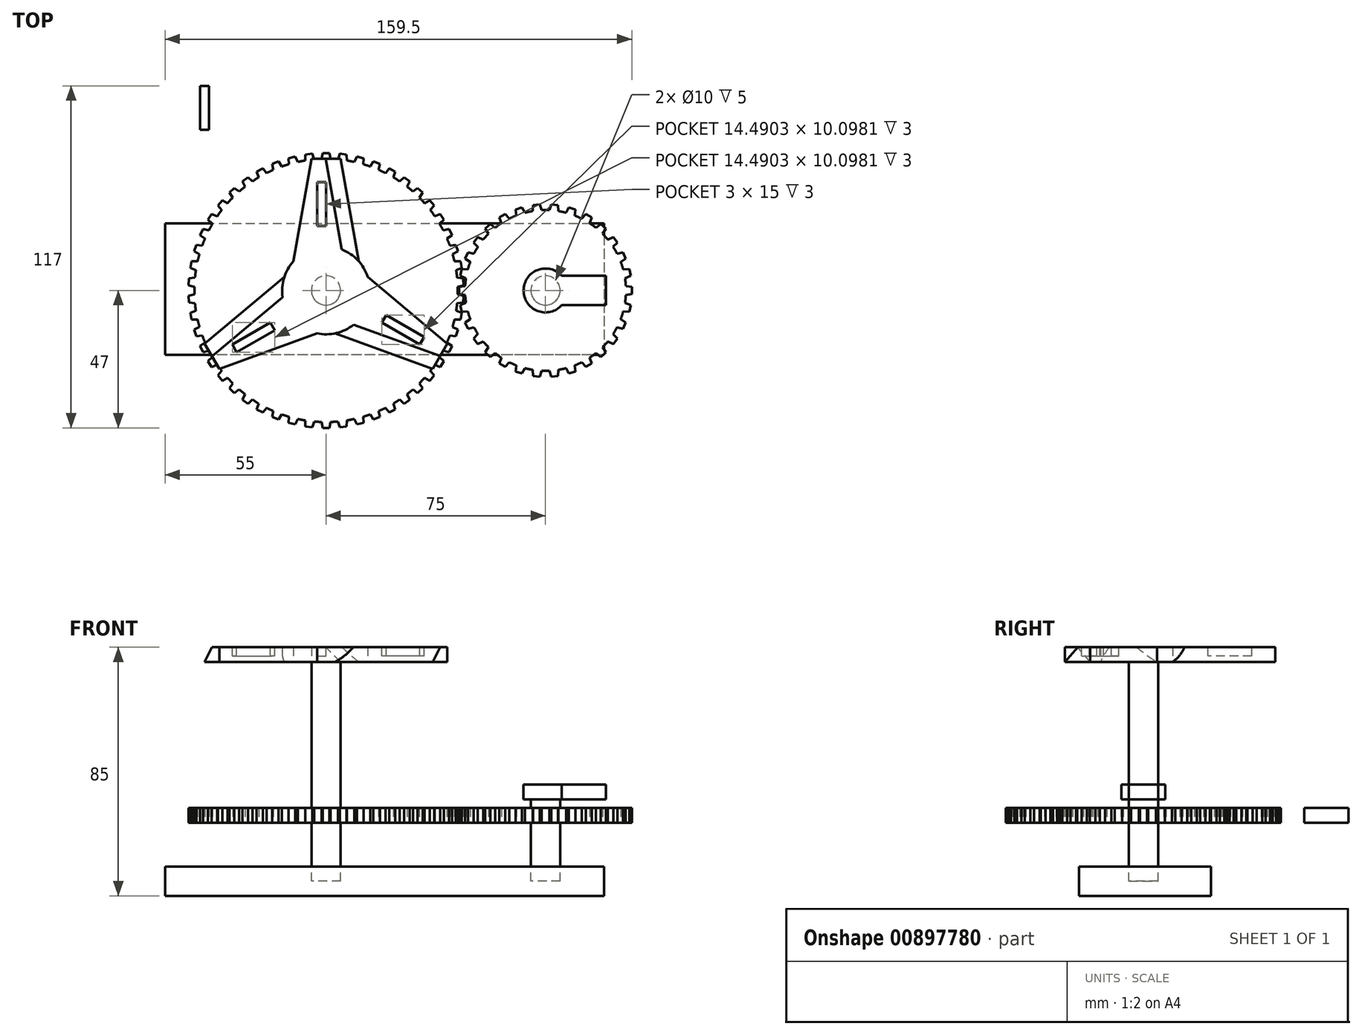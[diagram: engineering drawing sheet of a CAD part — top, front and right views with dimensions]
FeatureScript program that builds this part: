
annotation { "Feature Type Name" : "Feature", "Feature Type Description" : "" }
export const myFeature = defineFeature(function(context is Context, id is Id, definition is map)
    precondition{}
    {
        {
            var Q0;
            Q0=qCreatedBy(makeId("Top.planeOp"),FACE);
            var sketch = newSketch(context, id + "F0", { "sketchPlane" : qUnion([Q0])});
            skCircle(sketch, "E0", {"center": v(0, 0) * mm, "radius": 45 * mm});
            skLineSegment(sketch, "E1", {"start": v(0, 47) * mm, "end": v(1.18, 47) * mm});
            skLineSegment(sketch, "E2", {"start": v(1.18, 47) * mm, "end": v(1.54, 44.97) * mm});
            skLineSegment(sketch, "E3.MirrorCS", {"start": v(0, 47) * mm, "end": v(-1.18, 47) * mm});
            skLineSegment(sketch, "E4.MirrorCS", {"start": v(-1.18, 47) * mm, "end": v(-1.54, 44.97) * mm});
            skLineSegment(sketch, "E5.1.0", {"start": v(-7.06, 46.48) * mm, "end": v(-7.16, 44.43) * mm});
            skLineSegment(sketch, "E5.1.1", {"start": v(-5.9, 46.63) * mm, "end": v(-7.06, 46.48) * mm});
            skLineSegment(sketch, "E5.1.2", {"start": v(-5.9, 46.63) * mm, "end": v(-4.72, 46.78) * mm});
            skLineSegment(sketch, "E5.1.3", {"start": v(-4.72, 46.78) * mm, "end": v(-4.11, 44.81) * mm});
            skLineSegment(sketch, "E5.2.0", {"start": v(-12.83, 45.23) * mm, "end": v(-12.67, 43.18) * mm});
            skLineSegment(sketch, "E5.2.1", {"start": v(-11.69, 45.52) * mm, "end": v(-12.83, 45.23) * mm});
            skLineSegment(sketch, "E5.2.2", {"start": v(-11.69, 45.52) * mm, "end": v(-10.55, 45.82) * mm});
            skLineSegment(sketch, "E5.2.3", {"start": v(-10.55, 45.82) * mm, "end": v(-9.7, 43.94) * mm});
            skLineSegment(sketch, "E6.2.3.0", {"start": v(-18.4, 43.27) * mm, "end": v(-17.98, 41.25) * mm});
            skLineSegment(sketch, "E6.3.3.0", {"start": v(-17.3, 43.7) * mm, "end": v(-18.4, 43.27) * mm});
            skLineSegment(sketch, "E6.6.3.0", {"start": v(-17.3, 43.7) * mm, "end": v(-16.2, 44.13) * mm});
            skLineSegment(sketch, "E6.9.3.0", {"start": v(-16.2, 44.13) * mm, "end": v(-15.13, 42.38) * mm});
            skLineSegment(sketch, "E6.2.4.0", {"start": v(-23.67, 40.62) * mm, "end": v(-23.01, 38.67) * mm});
            skLineSegment(sketch, "E6.3.4.0", {"start": v(-22.64, 41.19) * mm, "end": v(-23.67, 40.62) * mm});
            skLineSegment(sketch, "E6.6.4.0", {"start": v(-22.64, 41.19) * mm, "end": v(-21.61, 41.75) * mm});
            skLineSegment(sketch, "E6.9.4.0", {"start": v(-21.61, 41.75) * mm, "end": v(-20.32, 40.15) * mm});
            skLineSegment(sketch, "E6.2.5.0", {"start": v(-28.58, 37.33) * mm, "end": v(-27.68, 35.48) * mm});
            skLineSegment(sketch, "E6.3.5.0", {"start": v(-27.63, 38.02) * mm, "end": v(-28.58, 37.33) * mm});
            skLineSegment(sketch, "E6.6.5.0", {"start": v(-27.63, 38.02) * mm, "end": v(-26.67, 38.72) * mm});
            skLineSegment(sketch, "E6.9.5.0", {"start": v(-26.67, 38.72) * mm, "end": v(-25.2, 37.29) * mm});
            skLineSegment(sketch, "E6.2.6.0", {"start": v(-33.03, 33.46) * mm, "end": v(-31.9, 31.73) * mm});
            skLineSegment(sketch, "E6.3.6.0", {"start": v(-32.17, 34.26) * mm, "end": v(-33.03, 33.46) * mm});
            skLineSegment(sketch, "E6.6.6.0", {"start": v(-32.17, 34.26) * mm, "end": v(-31.31, 35.07) * mm});
            skLineSegment(sketch, "E6.9.6.0", {"start": v(-31.31, 35.07) * mm, "end": v(-29.67, 33.84) * mm});
            skLineSegment(sketch, "E6.2.7.0", {"start": v(-36.97, 29.05) * mm, "end": v(-35.63, 27.48) * mm});
            skLineSegment(sketch, "E6.3.7.0", {"start": v(-36.21, 29.96) * mm, "end": v(-36.97, 29.05) * mm});
            skLineSegment(sketch, "E6.6.7.0", {"start": v(-36.21, 29.96) * mm, "end": v(-35.46, 30.87) * mm});
            skLineSegment(sketch, "E6.9.7.0", {"start": v(-35.46, 30.87) * mm, "end": v(-33.67, 29.85) * mm});
            skLineSegment(sketch, "E6.2.8.0", {"start": v(-40.31, 24.19) * mm, "end": v(-38.8, 22.8) * mm});
            skLineSegment(sketch, "E6.3.8.0", {"start": v(-39.68, 25.18) * mm, "end": v(-40.31, 24.19) * mm});
            skLineSegment(sketch, "E6.6.8.0", {"start": v(-39.68, 25.18) * mm, "end": v(-39.05, 26.18) * mm});
            skLineSegment(sketch, "E6.9.8.0", {"start": v(-39.05, 26.18) * mm, "end": v(-37.15, 25.4) * mm});
            skLineSegment(sketch, "E6.2.9.0", {"start": v(-43.03, 18.95) * mm, "end": v(-41.35, 17.76) * mm});
            skLineSegment(sketch, "E6.3.9.0", {"start": v(-42.53, 20.01) * mm, "end": v(-43.03, 18.95) * mm});
            skLineSegment(sketch, "E6.6.9.0", {"start": v(-42.53, 20.01) * mm, "end": v(-42.03, 21.08) * mm});
            skLineSegment(sketch, "E6.9.9.0", {"start": v(-42.03, 21.08) * mm, "end": v(-40.04, 20.54) * mm});
            skLineSegment(sketch, "E6.2.10.0", {"start": v(-45.06, 13.4) * mm, "end": v(-43.25, 12.44) * mm});
            skLineSegment(sketch, "E6.3.10.0", {"start": v(-44.7, 14.52) * mm, "end": v(-45.06, 13.4) * mm});
            skLineSegment(sketch, "E6.6.10.0", {"start": v(-44.7, 14.52) * mm, "end": v(-44.34, 15.64) * mm});
            skLineSegment(sketch, "E6.9.10.0", {"start": v(-44.34, 15.64) * mm, "end": v(-42.3, 15.36) * mm});
            skLineSegment(sketch, "E6.2.11.0", {"start": v(-46.39, 7.65) * mm, "end": v(-44.46, 6.92) * mm});
            skLineSegment(sketch, "E6.3.11.0", {"start": v(-46.17, 8.8) * mm, "end": v(-46.39, 7.65) * mm});
            skLineSegment(sketch, "E6.6.11.0", {"start": v(-46.17, 8.8) * mm, "end": v(-45.95, 9.96) * mm});
            skLineSegment(sketch, "E6.9.11.0", {"start": v(-45.95, 9.96) * mm, "end": v(-43.89, 9.94) * mm});
            skLineSegment(sketch, "E6.2.12.0", {"start": v(-46.98, 1.78) * mm, "end": v(-44.98, 1.3) * mm});
            skLineSegment(sketch, "E6.3.12.0", {"start": v(-46.9, 2.95) * mm, "end": v(-46.98, 1.78) * mm});
            skLineSegment(sketch, "E6.6.12.0", {"start": v(-46.9, 2.95) * mm, "end": v(-46.83, 4.13) * mm});
            skLineSegment(sketch, "E6.9.12.0", {"start": v(-46.83, 4.13) * mm, "end": v(-44.79, 4.36) * mm});
            skLineSegment(sketch, "E6.2.13.0", {"start": v(-46.83, -4.13) * mm, "end": v(-44.79, -4.36) * mm});
            skLineSegment(sketch, "E6.3.13.0", {"start": v(-46.9, -2.95) * mm, "end": v(-46.83, -4.13) * mm});
            skLineSegment(sketch, "E6.6.13.0", {"start": v(-46.9, -2.95) * mm, "end": v(-46.98, -1.78) * mm});
            skLineSegment(sketch, "E6.9.13.0", {"start": v(-46.98, -1.78) * mm, "end": v(-44.98, -1.3) * mm});
            skLineSegment(sketch, "E6.2.14.0", {"start": v(-45.95, -9.96) * mm, "end": v(-43.89, -9.94) * mm});
            skLineSegment(sketch, "E6.3.14.0", {"start": v(-46.17, -8.8) * mm, "end": v(-45.95, -9.96) * mm});
            skLineSegment(sketch, "E6.6.14.0", {"start": v(-46.17, -8.8) * mm, "end": v(-46.39, -7.65) * mm});
            skLineSegment(sketch, "E6.9.14.0", {"start": v(-46.39, -7.65) * mm, "end": v(-44.46, -6.92) * mm});
            skLineSegment(sketch, "E6.2.15.0", {"start": v(-44.34, -15.64) * mm, "end": v(-42.3, -15.36) * mm});
            skLineSegment(sketch, "E6.3.15.0", {"start": v(-44.7, -14.52) * mm, "end": v(-44.34, -15.64) * mm});
            skLineSegment(sketch, "E6.6.15.0", {"start": v(-44.7, -14.52) * mm, "end": v(-45.06, -13.4) * mm});
            skLineSegment(sketch, "E6.9.15.0", {"start": v(-45.06, -13.4) * mm, "end": v(-43.25, -12.44) * mm});
            skLineSegment(sketch, "E6.2.16.0", {"start": v(-42.03, -21.08) * mm, "end": v(-40.04, -20.54) * mm});
            skLineSegment(sketch, "E6.3.16.0", {"start": v(-42.53, -20.01) * mm, "end": v(-42.03, -21.08) * mm});
            skLineSegment(sketch, "E6.6.16.0", {"start": v(-42.53, -20.01) * mm, "end": v(-43.03, -18.95) * mm});
            skLineSegment(sketch, "E6.9.16.0", {"start": v(-43.03, -18.95) * mm, "end": v(-41.35, -17.76) * mm});
            skLineSegment(sketch, "E6.2.17.0", {"start": v(-39.05, -26.18) * mm, "end": v(-37.15, -25.4) * mm});
            skLineSegment(sketch, "E6.3.17.0", {"start": v(-39.68, -25.18) * mm, "end": v(-39.05, -26.18) * mm});
            skLineSegment(sketch, "E6.6.17.0", {"start": v(-39.68, -25.18) * mm, "end": v(-40.31, -24.19) * mm});
            skLineSegment(sketch, "E6.9.17.0", {"start": v(-40.31, -24.19) * mm, "end": v(-38.8, -22.8) * mm});
            skLineSegment(sketch, "E6.2.18.0", {"start": v(-35.46, -30.87) * mm, "end": v(-33.67, -29.85) * mm});
            skLineSegment(sketch, "E6.3.18.0", {"start": v(-36.21, -29.96) * mm, "end": v(-35.46, -30.87) * mm});
            skLineSegment(sketch, "E6.6.18.0", {"start": v(-36.21, -29.96) * mm, "end": v(-36.97, -29.05) * mm});
            skLineSegment(sketch, "E6.9.18.0", {"start": v(-36.97, -29.05) * mm, "end": v(-35.63, -27.48) * mm});
            skLineSegment(sketch, "E6.2.19.0", {"start": v(-31.31, -35.07) * mm, "end": v(-29.67, -33.84) * mm});
            skLineSegment(sketch, "E6.3.19.0", {"start": v(-32.17, -34.26) * mm, "end": v(-31.31, -35.07) * mm});
            skLineSegment(sketch, "E6.6.19.0", {"start": v(-32.17, -34.26) * mm, "end": v(-33.03, -33.46) * mm});
            skLineSegment(sketch, "E6.9.19.0", {"start": v(-33.03, -33.46) * mm, "end": v(-31.9, -31.73) * mm});
            skLineSegment(sketch, "E6.2.20.0", {"start": v(-26.67, -38.72) * mm, "end": v(-25.2, -37.29) * mm});
            skLineSegment(sketch, "E6.3.20.0", {"start": v(-27.63, -38.02) * mm, "end": v(-26.67, -38.72) * mm});
            skLineSegment(sketch, "E6.6.20.0", {"start": v(-27.63, -38.02) * mm, "end": v(-28.58, -37.33) * mm});
            skLineSegment(sketch, "E6.9.20.0", {"start": v(-28.58, -37.33) * mm, "end": v(-27.68, -35.48) * mm});
            skLineSegment(sketch, "E6.2.21.0", {"start": v(-21.61, -41.75) * mm, "end": v(-20.32, -40.15) * mm});
            skLineSegment(sketch, "E6.3.21.0", {"start": v(-22.64, -41.19) * mm, "end": v(-21.61, -41.75) * mm});
            skLineSegment(sketch, "E6.6.21.0", {"start": v(-22.64, -41.19) * mm, "end": v(-23.67, -40.62) * mm});
            skLineSegment(sketch, "E6.9.21.0", {"start": v(-23.67, -40.62) * mm, "end": v(-23.01, -38.67) * mm});
            skLineSegment(sketch, "E6.2.22.0", {"start": v(-16.2, -44.13) * mm, "end": v(-15.13, -42.38) * mm});
            skLineSegment(sketch, "E6.3.22.0", {"start": v(-17.3, -43.7) * mm, "end": v(-16.2, -44.13) * mm});
            skLineSegment(sketch, "E6.6.22.0", {"start": v(-17.3, -43.7) * mm, "end": v(-18.4, -43.27) * mm});
            skLineSegment(sketch, "E6.9.22.0", {"start": v(-18.4, -43.27) * mm, "end": v(-17.98, -41.25) * mm});
            skLineSegment(sketch, "E6.2.23.0", {"start": v(-10.55, -45.82) * mm, "end": v(-9.7, -43.94) * mm});
            skLineSegment(sketch, "E6.3.23.0", {"start": v(-11.69, -45.52) * mm, "end": v(-10.55, -45.82) * mm});
            skLineSegment(sketch, "E6.6.23.0", {"start": v(-11.69, -45.52) * mm, "end": v(-12.83, -45.23) * mm});
            skLineSegment(sketch, "E6.9.23.0", {"start": v(-12.83, -45.23) * mm, "end": v(-12.67, -43.18) * mm});
            skLineSegment(sketch, "E6.2.24.0", {"start": v(-4.72, -46.78) * mm, "end": v(-4.11, -44.81) * mm});
            skLineSegment(sketch, "E6.3.24.0", {"start": v(-5.9, -46.63) * mm, "end": v(-4.72, -46.78) * mm});
            skLineSegment(sketch, "E6.6.24.0", {"start": v(-5.9, -46.63) * mm, "end": v(-7.06, -46.48) * mm});
            skLineSegment(sketch, "E6.9.24.0", {"start": v(-7.06, -46.48) * mm, "end": v(-7.16, -44.43) * mm});
            skLineSegment(sketch, "E6.2.25.0", {"start": v(1.18, -47) * mm, "end": v(1.54, -44.97) * mm});
            skLineSegment(sketch, "E6.3.25.0", {"start": v(0, -47) * mm, "end": v(1.18, -47) * mm});
            skLineSegment(sketch, "E6.6.25.0", {"start": v(0, -47) * mm, "end": v(-1.18, -47) * mm});
            skLineSegment(sketch, "E6.9.25.0", {"start": v(-1.18, -47) * mm, "end": v(-1.54, -44.97) * mm});
            skLineSegment(sketch, "E6.2.26.0", {"start": v(7.06, -46.48) * mm, "end": v(7.16, -44.43) * mm});
            skLineSegment(sketch, "E6.3.26.0", {"start": v(5.9, -46.63) * mm, "end": v(7.06, -46.48) * mm});
            skLineSegment(sketch, "E6.6.26.0", {"start": v(5.9, -46.63) * mm, "end": v(4.72, -46.78) * mm});
            skLineSegment(sketch, "E6.9.26.0", {"start": v(4.72, -46.78) * mm, "end": v(4.11, -44.81) * mm});
            skLineSegment(sketch, "E6.2.27.0", {"start": v(12.83, -45.23) * mm, "end": v(12.67, -43.18) * mm});
            skLineSegment(sketch, "E6.3.27.0", {"start": v(11.69, -45.52) * mm, "end": v(12.83, -45.23) * mm});
            skLineSegment(sketch, "E6.6.27.0", {"start": v(11.69, -45.52) * mm, "end": v(10.55, -45.82) * mm});
            skLineSegment(sketch, "E6.9.27.0", {"start": v(10.55, -45.82) * mm, "end": v(9.7, -43.94) * mm});
            skLineSegment(sketch, "E6.2.28.0", {"start": v(18.4, -43.27) * mm, "end": v(17.98, -41.25) * mm});
            skLineSegment(sketch, "E6.3.28.0", {"start": v(17.3, -43.7) * mm, "end": v(18.4, -43.27) * mm});
            skLineSegment(sketch, "E6.6.28.0", {"start": v(17.3, -43.7) * mm, "end": v(16.2, -44.13) * mm});
            skLineSegment(sketch, "E6.9.28.0", {"start": v(16.2, -44.13) * mm, "end": v(15.13, -42.38) * mm});
            skLineSegment(sketch, "E6.2.29.0", {"start": v(23.67, -40.62) * mm, "end": v(23.01, -38.67) * mm});
            skLineSegment(sketch, "E6.3.29.0", {"start": v(22.64, -41.19) * mm, "end": v(23.67, -40.62) * mm});
            skLineSegment(sketch, "E6.6.29.0", {"start": v(22.64, -41.19) * mm, "end": v(21.61, -41.75) * mm});
            skLineSegment(sketch, "E6.9.29.0", {"start": v(21.61, -41.75) * mm, "end": v(20.32, -40.15) * mm});
            skLineSegment(sketch, "E7.2.30.0", {"start": v(28.58, -37.33) * mm, "end": v(27.68, -35.48) * mm});
            skLineSegment(sketch, "E7.3.30.0", {"start": v(27.63, -38.02) * mm, "end": v(28.58, -37.33) * mm});
            skLineSegment(sketch, "E7.6.30.0", {"start": v(27.63, -38.02) * mm, "end": v(26.67, -38.72) * mm});
            skLineSegment(sketch, "E7.9.30.0", {"start": v(26.67, -38.72) * mm, "end": v(25.2, -37.29) * mm});
            skLineSegment(sketch, "E7.2.31.0", {"start": v(33.03, -33.46) * mm, "end": v(31.9, -31.73) * mm});
            skLineSegment(sketch, "E7.3.31.0", {"start": v(32.17, -34.26) * mm, "end": v(33.03, -33.46) * mm});
            skLineSegment(sketch, "E7.6.31.0", {"start": v(32.17, -34.26) * mm, "end": v(31.31, -35.07) * mm});
            skLineSegment(sketch, "E7.9.31.0", {"start": v(31.31, -35.07) * mm, "end": v(29.67, -33.84) * mm});
            skLineSegment(sketch, "E7.2.32.0", {"start": v(36.97, -29.05) * mm, "end": v(35.63, -27.48) * mm});
            skLineSegment(sketch, "E7.3.32.0", {"start": v(36.21, -29.96) * mm, "end": v(36.97, -29.05) * mm});
            skLineSegment(sketch, "E7.6.32.0", {"start": v(36.21, -29.96) * mm, "end": v(35.46, -30.87) * mm});
            skLineSegment(sketch, "E7.9.32.0", {"start": v(35.46, -30.87) * mm, "end": v(33.67, -29.85) * mm});
            skLineSegment(sketch, "E7.2.33.0", {"start": v(40.31, -24.19) * mm, "end": v(38.8, -22.8) * mm});
            skLineSegment(sketch, "E7.3.33.0", {"start": v(39.68, -25.18) * mm, "end": v(40.31, -24.19) * mm});
            skLineSegment(sketch, "E7.6.33.0", {"start": v(39.68, -25.18) * mm, "end": v(39.05, -26.18) * mm});
            skLineSegment(sketch, "E7.9.33.0", {"start": v(39.05, -26.18) * mm, "end": v(37.15, -25.4) * mm});
            skLineSegment(sketch, "E7.2.34.0", {"start": v(43.03, -18.95) * mm, "end": v(41.35, -17.76) * mm});
            skLineSegment(sketch, "E7.3.34.0", {"start": v(42.53, -20.01) * mm, "end": v(43.03, -18.95) * mm});
            skLineSegment(sketch, "E7.6.34.0", {"start": v(42.53, -20.01) * mm, "end": v(42.03, -21.08) * mm});
            skLineSegment(sketch, "E7.9.34.0", {"start": v(42.03, -21.08) * mm, "end": v(40.04, -20.54) * mm});
            skLineSegment(sketch, "E7.2.35.0", {"start": v(45.06, -13.4) * mm, "end": v(43.25, -12.44) * mm});
            skLineSegment(sketch, "E7.3.35.0", {"start": v(44.7, -14.52) * mm, "end": v(45.06, -13.4) * mm});
            skLineSegment(sketch, "E7.6.35.0", {"start": v(44.7, -14.52) * mm, "end": v(44.34, -15.64) * mm});
            skLineSegment(sketch, "E7.9.35.0", {"start": v(44.34, -15.64) * mm, "end": v(42.3, -15.36) * mm});
            skLineSegment(sketch, "E7.2.36.0", {"start": v(46.39, -7.65) * mm, "end": v(44.46, -6.92) * mm});
            skLineSegment(sketch, "E7.3.36.0", {"start": v(46.17, -8.8) * mm, "end": v(46.39, -7.65) * mm});
            skLineSegment(sketch, "E7.6.36.0", {"start": v(46.17, -8.8) * mm, "end": v(45.95, -9.96) * mm});
            skLineSegment(sketch, "E7.9.36.0", {"start": v(45.95, -9.96) * mm, "end": v(43.89, -9.94) * mm});
            skLineSegment(sketch, "E7.2.37.0", {"start": v(46.98, -1.78) * mm, "end": v(44.98, -1.3) * mm});
            skLineSegment(sketch, "E7.3.37.0", {"start": v(46.9, -2.95) * mm, "end": v(46.98, -1.78) * mm});
            skLineSegment(sketch, "E7.6.37.0", {"start": v(46.9, -2.95) * mm, "end": v(46.83, -4.13) * mm});
            skLineSegment(sketch, "E7.9.37.0", {"start": v(46.83, -4.13) * mm, "end": v(44.79, -4.36) * mm});
            skLineSegment(sketch, "E7.2.38.0", {"start": v(46.83, 4.13) * mm, "end": v(44.79, 4.36) * mm});
            skLineSegment(sketch, "E7.3.38.0", {"start": v(46.9, 2.95) * mm, "end": v(46.83, 4.13) * mm});
            skLineSegment(sketch, "E7.6.38.0", {"start": v(46.9, 2.95) * mm, "end": v(46.98, 1.78) * mm});
            skLineSegment(sketch, "E7.9.38.0", {"start": v(46.98, 1.78) * mm, "end": v(44.98, 1.3) * mm});
            skLineSegment(sketch, "E7.2.39.0", {"start": v(45.95, 9.96) * mm, "end": v(43.89, 9.94) * mm});
            skLineSegment(sketch, "E7.3.39.0", {"start": v(46.17, 8.8) * mm, "end": v(45.95, 9.96) * mm});
            skLineSegment(sketch, "E7.6.39.0", {"start": v(46.17, 8.8) * mm, "end": v(46.39, 7.65) * mm});
            skLineSegment(sketch, "E7.9.39.0", {"start": v(46.39, 7.65) * mm, "end": v(44.46, 6.92) * mm});
            skLineSegment(sketch, "E7.2.40.0", {"start": v(44.34, 15.64) * mm, "end": v(42.3, 15.36) * mm});
            skLineSegment(sketch, "E7.3.40.0", {"start": v(44.7, 14.52) * mm, "end": v(44.34, 15.64) * mm});
            skLineSegment(sketch, "E7.6.40.0", {"start": v(44.7, 14.52) * mm, "end": v(45.06, 13.4) * mm});
            skLineSegment(sketch, "E7.9.40.0", {"start": v(45.06, 13.4) * mm, "end": v(43.25, 12.44) * mm});
            skLineSegment(sketch, "E7.2.41.0", {"start": v(42.03, 21.08) * mm, "end": v(40.04, 20.54) * mm});
            skLineSegment(sketch, "E7.3.41.0", {"start": v(42.53, 20.01) * mm, "end": v(42.03, 21.08) * mm});
            skLineSegment(sketch, "E7.6.41.0", {"start": v(42.53, 20.01) * mm, "end": v(43.03, 18.95) * mm});
            skLineSegment(sketch, "E7.9.41.0", {"start": v(43.03, 18.95) * mm, "end": v(41.35, 17.76) * mm});
            skLineSegment(sketch, "E7.2.42.0", {"start": v(39.05, 26.18) * mm, "end": v(37.15, 25.4) * mm});
            skLineSegment(sketch, "E7.3.42.0", {"start": v(39.68, 25.18) * mm, "end": v(39.05, 26.18) * mm});
            skLineSegment(sketch, "E7.6.42.0", {"start": v(39.68, 25.18) * mm, "end": v(40.31, 24.19) * mm});
            skLineSegment(sketch, "E7.9.42.0", {"start": v(40.31, 24.19) * mm, "end": v(38.8, 22.8) * mm});
            skLineSegment(sketch, "E7.2.43.0", {"start": v(35.46, 30.87) * mm, "end": v(33.67, 29.85) * mm});
            skLineSegment(sketch, "E7.3.43.0", {"start": v(36.21, 29.96) * mm, "end": v(35.46, 30.87) * mm});
            skLineSegment(sketch, "E7.6.43.0", {"start": v(36.21, 29.96) * mm, "end": v(36.97, 29.05) * mm});
            skLineSegment(sketch, "E7.9.43.0", {"start": v(36.97, 29.05) * mm, "end": v(35.63, 27.48) * mm});
            skLineSegment(sketch, "E7.2.44.0", {"start": v(31.31, 35.07) * mm, "end": v(29.67, 33.84) * mm});
            skLineSegment(sketch, "E7.3.44.0", {"start": v(32.17, 34.26) * mm, "end": v(31.31, 35.07) * mm});
            skLineSegment(sketch, "E7.6.44.0", {"start": v(32.17, 34.26) * mm, "end": v(33.03, 33.46) * mm});
            skLineSegment(sketch, "E7.9.44.0", {"start": v(33.03, 33.46) * mm, "end": v(31.9, 31.73) * mm});
            skLineSegment(sketch, "E7.2.45.0", {"start": v(26.67, 38.72) * mm, "end": v(25.2, 37.29) * mm});
            skLineSegment(sketch, "E7.3.45.0", {"start": v(27.63, 38.02) * mm, "end": v(26.67, 38.72) * mm});
            skLineSegment(sketch, "E7.6.45.0", {"start": v(27.63, 38.02) * mm, "end": v(28.58, 37.33) * mm});
            skLineSegment(sketch, "E7.9.45.0", {"start": v(28.58, 37.33) * mm, "end": v(27.68, 35.48) * mm});
            skLineSegment(sketch, "E7.2.46.0", {"start": v(21.61, 41.75) * mm, "end": v(20.32, 40.15) * mm});
            skLineSegment(sketch, "E7.3.46.0", {"start": v(22.64, 41.19) * mm, "end": v(21.61, 41.75) * mm});
            skLineSegment(sketch, "E7.6.46.0", {"start": v(22.64, 41.19) * mm, "end": v(23.67, 40.62) * mm});
            skLineSegment(sketch, "E7.9.46.0", {"start": v(23.67, 40.62) * mm, "end": v(23.01, 38.67) * mm});
            skLineSegment(sketch, "E7.2.47.0", {"start": v(16.2, 44.13) * mm, "end": v(15.13, 42.38) * mm});
            skLineSegment(sketch, "E7.3.47.0", {"start": v(17.3, 43.7) * mm, "end": v(16.2, 44.13) * mm});
            skLineSegment(sketch, "E7.6.47.0", {"start": v(17.3, 43.7) * mm, "end": v(18.4, 43.27) * mm});
            skLineSegment(sketch, "E7.9.47.0", {"start": v(18.4, 43.27) * mm, "end": v(17.98, 41.25) * mm});
            skLineSegment(sketch, "E7.2.48.0", {"start": v(10.55, 45.82) * mm, "end": v(9.7, 43.94) * mm});
            skLineSegment(sketch, "E7.3.48.0", {"start": v(11.69, 45.52) * mm, "end": v(10.55, 45.82) * mm});
            skLineSegment(sketch, "E7.6.48.0", {"start": v(11.69, 45.52) * mm, "end": v(12.83, 45.23) * mm});
            skLineSegment(sketch, "E7.9.48.0", {"start": v(12.83, 45.23) * mm, "end": v(12.67, 43.18) * mm});
            skLineSegment(sketch, "E7.2.49.0", {"start": v(4.72, 46.78) * mm, "end": v(4.11, 44.81) * mm});
            skLineSegment(sketch, "E7.3.49.0", {"start": v(5.9, 46.63) * mm, "end": v(4.72, 46.78) * mm});
            skLineSegment(sketch, "E7.6.49.0", {"start": v(5.9, 46.63) * mm, "end": v(7.06, 46.48) * mm});
            skLineSegment(sketch, "E7.9.49.0", {"start": v(7.06, 46.48) * mm, "end": v(7.16, 44.43) * mm});
            skSolve(sketch);
        }
        {
            var Q0;
            Q0 = qSketchRegion(id + "F0", true);
            extrude(context, id + "F1", {"entities" : qUnion([Q0]), "depth" : 5 * mm, "offsetDistance" : 25 * mm});
        }
        {
            var Q0;
            Q0=qCreatedBy(makeId("Top.planeOp"),FACE);
            var sketch = newSketch(context, id + "F2", { "sketchPlane" : qUnion([Q0])});
            skCircle(sketch, "E8", {"center": v(75, 0) * mm, "radius": 27.5 * mm});
            skLineSegment(sketch, "E9", {"start": v(45.5, 0) * mm, "end": v(45.5, 1.18) * mm});
            skLineSegment(sketch, "E10", {"start": v(45.5, 1.18) * mm, "end": v(47.54, 1.54) * mm});
            skLineSegment(sketch, "E11.MirrorCS", {"start": v(45.5, 0) * mm, "end": v(45.5, -1.18) * mm});
            skLineSegment(sketch, "E12.MirrorCS", {"start": v(45.5, -1.18) * mm, "end": v(47.54, -1.54) * mm});
            skLineSegment(sketch, "E13.1.0", {"start": v(46.14, -6.13) * mm, "end": v(45.9, -4.98) * mm});
            skLineSegment(sketch, "E13.1.1", {"start": v(45.9, -4.98) * mm, "end": v(47.82, -4.2) * mm});
            skLineSegment(sketch, "E13.1.2", {"start": v(46.14, -6.13) * mm, "end": v(46.39, -7.29) * mm});
            skLineSegment(sketch, "E13.1.3", {"start": v(46.39, -7.29) * mm, "end": v(48.46, -7.21) * mm});
            skLineSegment(sketch, "E14.1.2.0", {"start": v(48.05, -12) * mm, "end": v(47.57, -10.92) * mm});
            skLineSegment(sketch, "E14.3.2.0", {"start": v(47.57, -10.92) * mm, "end": v(49.3, -9.76) * mm});
            skLineSegment(sketch, "E14.6.2.0", {"start": v(48.05, -12) * mm, "end": v(48.53, -13.07) * mm});
            skLineSegment(sketch, "E14.9.2.0", {"start": v(48.53, -13.07) * mm, "end": v(50.54, -12.57) * mm});
            skLineSegment(sketch, "E14.1.3.0", {"start": v(51.13, -17.34) * mm, "end": v(50.44, -16.39) * mm});
            skLineSegment(sketch, "E14.3.3.0", {"start": v(50.44, -16.39) * mm, "end": v(51.88, -14.9) * mm});
            skLineSegment(sketch, "E14.6.3.0", {"start": v(51.13, -17.34) * mm, "end": v(51.83, -18.3) * mm});
            skLineSegment(sketch, "E14.9.3.0", {"start": v(51.83, -18.3) * mm, "end": v(53.7, -17.38) * mm});
            skLineSegment(sketch, "E14.1.4.0", {"start": v(55.26, -21.92) * mm, "end": v(54.39, -21.13) * mm});
            skLineSegment(sketch, "E14.3.4.0", {"start": v(54.39, -21.13) * mm, "end": v(55.48, -19.38) * mm});
            skLineSegment(sketch, "E14.6.4.0", {"start": v(55.26, -21.92) * mm, "end": v(56.14, -22.71) * mm});
            skLineSegment(sketch, "E14.9.4.0", {"start": v(56.14, -22.71) * mm, "end": v(57.77, -21.43) * mm});
            skLineSegment(sketch, "E14.1.5.0", {"start": v(60.25, -25.55) * mm, "end": v(59.23, -24.96) * mm});
            skLineSegment(sketch, "E14.3.5.0", {"start": v(59.23, -24.96) * mm, "end": v(59.94, -23) * mm});
            skLineSegment(sketch, "E14.6.5.0", {"start": v(60.25, -25.55) * mm, "end": v(61.27, -26.14) * mm});
            skLineSegment(sketch, "E14.9.5.0", {"start": v(61.27, -26.14) * mm, "end": v(62.6, -24.55) * mm});
            skLineSegment(sketch, "E14.1.6.0", {"start": v(65.88, -28.06) * mm, "end": v(64.76, -27.7) * mm});
            skLineSegment(sketch, "E14.3.6.0", {"start": v(64.76, -27.7) * mm, "end": v(65.05, -25.64) * mm});
            skLineSegment(sketch, "E14.6.6.0", {"start": v(65.88, -28.06) * mm, "end": v(67, -28.42) * mm});
            skLineSegment(sketch, "E14.9.6.0", {"start": v(67, -28.42) * mm, "end": v(67.98, -26.59) * mm});
            skLineSegment(sketch, "E14.1.7.0", {"start": v(71.92, -29.34) * mm, "end": v(70.74, -29.22) * mm});
            skLineSegment(sketch, "E14.3.7.0", {"start": v(70.74, -29.22) * mm, "end": v(70.6, -27.15) * mm});
            skLineSegment(sketch, "E14.6.7.0", {"start": v(71.92, -29.34) * mm, "end": v(73.09, -29.46) * mm});
            skLineSegment(sketch, "E14.9.7.0", {"start": v(73.09, -29.46) * mm, "end": v(73.66, -27.47) * mm});
            skLineSegment(sketch, "E14.1.8.0", {"start": v(78.08, -29.34) * mm, "end": v(76.91, -29.46) * mm});
            skLineSegment(sketch, "E14.3.8.0", {"start": v(76.91, -29.46) * mm, "end": v(76.34, -27.47) * mm});
            skLineSegment(sketch, "E14.6.8.0", {"start": v(78.08, -29.34) * mm, "end": v(79.26, -29.22) * mm});
            skLineSegment(sketch, "E14.9.8.0", {"start": v(79.26, -29.22) * mm, "end": v(79.4, -27.15) * mm});
            skLineSegment(sketch, "E14.1.9.0", {"start": v(84.12, -28.06) * mm, "end": v(83, -28.42) * mm});
            skLineSegment(sketch, "E14.3.9.0", {"start": v(83, -28.42) * mm, "end": v(82.02, -26.59) * mm});
            skLineSegment(sketch, "E14.6.9.0", {"start": v(84.12, -28.06) * mm, "end": v(85.24, -27.7) * mm});
            skLineSegment(sketch, "E14.9.9.0", {"start": v(85.24, -27.7) * mm, "end": v(84.95, -25.64) * mm});
            skLineSegment(sketch, "E15.1.10.0", {"start": v(89.75, -25.55) * mm, "end": v(88.73, -26.14) * mm});
            skLineSegment(sketch, "E15.3.10.0", {"start": v(88.73, -26.14) * mm, "end": v(87.4, -24.55) * mm});
            skLineSegment(sketch, "E15.6.10.0", {"start": v(89.75, -25.55) * mm, "end": v(90.77, -24.96) * mm});
            skLineSegment(sketch, "E15.9.10.0", {"start": v(90.77, -24.96) * mm, "end": v(90.06, -23) * mm});
            skLineSegment(sketch, "E15.1.11.0", {"start": v(94.74, -21.92) * mm, "end": v(93.86, -22.71) * mm});
            skLineSegment(sketch, "E15.3.11.0", {"start": v(93.86, -22.71) * mm, "end": v(92.23, -21.43) * mm});
            skLineSegment(sketch, "E15.6.11.0", {"start": v(94.74, -21.92) * mm, "end": v(95.61, -21.13) * mm});
            skLineSegment(sketch, "E15.9.11.0", {"start": v(95.61, -21.13) * mm, "end": v(94.52, -19.38) * mm});
            skLineSegment(sketch, "E15.1.12.0", {"start": v(98.87, -17.34) * mm, "end": v(98.17, -18.3) * mm});
            skLineSegment(sketch, "E15.3.12.0", {"start": v(98.17, -18.3) * mm, "end": v(96.3, -17.38) * mm});
            skLineSegment(sketch, "E15.6.12.0", {"start": v(98.87, -17.34) * mm, "end": v(99.56, -16.39) * mm});
            skLineSegment(sketch, "E15.9.12.0", {"start": v(99.56, -16.39) * mm, "end": v(98.12, -14.9) * mm});
            skLineSegment(sketch, "E15.1.13.0", {"start": v(101.95, -12) * mm, "end": v(101.47, -13.07) * mm});
            skLineSegment(sketch, "E15.3.13.0", {"start": v(101.47, -13.07) * mm, "end": v(99.46, -12.57) * mm});
            skLineSegment(sketch, "E15.6.13.0", {"start": v(101.95, -12) * mm, "end": v(102.43, -10.92) * mm});
            skLineSegment(sketch, "E15.9.13.0", {"start": v(102.43, -10.92) * mm, "end": v(100.7, -9.76) * mm});
            skLineSegment(sketch, "E15.1.14.0", {"start": v(103.86, -6.13) * mm, "end": v(103.61, -7.29) * mm});
            skLineSegment(sketch, "E15.3.14.0", {"start": v(103.61, -7.29) * mm, "end": v(101.54, -7.21) * mm});
            skLineSegment(sketch, "E15.6.14.0", {"start": v(103.86, -6.13) * mm, "end": v(104.1, -4.98) * mm});
            skLineSegment(sketch, "E15.9.14.0", {"start": v(104.1, -4.98) * mm, "end": v(102.18, -4.2) * mm});
            skLineSegment(sketch, "E15.1.15.0", {"start": v(104.5, 0) * mm, "end": v(104.5, -1.18) * mm});
            skLineSegment(sketch, "E15.3.15.0", {"start": v(104.5, -1.18) * mm, "end": v(102.46, -1.54) * mm});
            skLineSegment(sketch, "E15.6.15.0", {"start": v(104.5, 0) * mm, "end": v(104.5, 1.18) * mm});
            skLineSegment(sketch, "E15.9.15.0", {"start": v(104.5, 1.18) * mm, "end": v(102.46, 1.54) * mm});
            skLineSegment(sketch, "E15.1.16.0", {"start": v(103.86, 6.13) * mm, "end": v(104.1, 4.98) * mm});
            skLineSegment(sketch, "E15.3.16.0", {"start": v(104.1, 4.98) * mm, "end": v(102.18, 4.2) * mm});
            skLineSegment(sketch, "E15.6.16.0", {"start": v(103.86, 6.13) * mm, "end": v(103.61, 7.29) * mm});
            skLineSegment(sketch, "E15.9.16.0", {"start": v(103.61, 7.29) * mm, "end": v(101.54, 7.21) * mm});
            skLineSegment(sketch, "E15.1.17.0", {"start": v(101.95, 12) * mm, "end": v(102.43, 10.92) * mm});
            skLineSegment(sketch, "E15.3.17.0", {"start": v(102.43, 10.92) * mm, "end": v(100.7, 9.76) * mm});
            skLineSegment(sketch, "E15.6.17.0", {"start": v(101.95, 12) * mm, "end": v(101.47, 13.07) * mm});
            skLineSegment(sketch, "E15.9.17.0", {"start": v(101.47, 13.07) * mm, "end": v(99.46, 12.57) * mm});
            skLineSegment(sketch, "E15.1.18.0", {"start": v(98.87, 17.34) * mm, "end": v(99.56, 16.39) * mm});
            skLineSegment(sketch, "E15.3.18.0", {"start": v(99.56, 16.39) * mm, "end": v(98.12, 14.9) * mm});
            skLineSegment(sketch, "E15.6.18.0", {"start": v(98.87, 17.34) * mm, "end": v(98.17, 18.3) * mm});
            skLineSegment(sketch, "E15.9.18.0", {"start": v(98.17, 18.3) * mm, "end": v(96.3, 17.38) * mm});
            skLineSegment(sketch, "E15.1.19.0", {"start": v(94.74, 21.92) * mm, "end": v(95.61, 21.13) * mm});
            skLineSegment(sketch, "E15.3.19.0", {"start": v(95.61, 21.13) * mm, "end": v(94.52, 19.38) * mm});
            skLineSegment(sketch, "E15.6.19.0", {"start": v(94.74, 21.92) * mm, "end": v(93.86, 22.71) * mm});
            skLineSegment(sketch, "E15.9.19.0", {"start": v(93.86, 22.71) * mm, "end": v(92.23, 21.43) * mm});
            skLineSegment(sketch, "E15.1.20.0", {"start": v(89.75, 25.55) * mm, "end": v(90.77, 24.96) * mm});
            skLineSegment(sketch, "E15.3.20.0", {"start": v(90.77, 24.96) * mm, "end": v(90.06, 23) * mm});
            skLineSegment(sketch, "E15.6.20.0", {"start": v(89.75, 25.55) * mm, "end": v(88.73, 26.14) * mm});
            skLineSegment(sketch, "E15.9.20.0", {"start": v(88.73, 26.14) * mm, "end": v(87.4, 24.55) * mm});
            skLineSegment(sketch, "E15.1.21.0", {"start": v(84.12, 28.06) * mm, "end": v(85.24, 27.7) * mm});
            skLineSegment(sketch, "E15.3.21.0", {"start": v(85.24, 27.7) * mm, "end": v(84.95, 25.64) * mm});
            skLineSegment(sketch, "E15.6.21.0", {"start": v(84.12, 28.06) * mm, "end": v(83, 28.42) * mm});
            skLineSegment(sketch, "E15.9.21.0", {"start": v(83, 28.42) * mm, "end": v(82.02, 26.59) * mm});
            skLineSegment(sketch, "E15.1.22.0", {"start": v(78.08, 29.34) * mm, "end": v(79.26, 29.22) * mm});
            skLineSegment(sketch, "E15.3.22.0", {"start": v(79.26, 29.22) * mm, "end": v(79.4, 27.15) * mm});
            skLineSegment(sketch, "E15.6.22.0", {"start": v(78.08, 29.34) * mm, "end": v(76.91, 29.46) * mm});
            skLineSegment(sketch, "E15.9.22.0", {"start": v(76.91, 29.46) * mm, "end": v(76.34, 27.47) * mm});
            skLineSegment(sketch, "E15.1.23.0", {"start": v(71.92, 29.34) * mm, "end": v(73.09, 29.46) * mm});
            skLineSegment(sketch, "E15.3.23.0", {"start": v(73.09, 29.46) * mm, "end": v(73.66, 27.47) * mm});
            skLineSegment(sketch, "E15.6.23.0", {"start": v(71.92, 29.34) * mm, "end": v(70.74, 29.22) * mm});
            skLineSegment(sketch, "E15.9.23.0", {"start": v(70.74, 29.22) * mm, "end": v(70.6, 27.15) * mm});
            skLineSegment(sketch, "E15.1.24.0", {"start": v(65.88, 28.06) * mm, "end": v(67, 28.42) * mm});
            skLineSegment(sketch, "E15.3.24.0", {"start": v(67, 28.42) * mm, "end": v(67.98, 26.59) * mm});
            skLineSegment(sketch, "E15.6.24.0", {"start": v(65.88, 28.06) * mm, "end": v(64.76, 27.7) * mm});
            skLineSegment(sketch, "E15.9.24.0", {"start": v(64.76, 27.7) * mm, "end": v(65.05, 25.64) * mm});
            skLineSegment(sketch, "E15.1.25.0", {"start": v(60.25, 25.55) * mm, "end": v(61.27, 26.14) * mm});
            skLineSegment(sketch, "E15.3.25.0", {"start": v(61.27, 26.14) * mm, "end": v(62.6, 24.55) * mm});
            skLineSegment(sketch, "E15.6.25.0", {"start": v(60.25, 25.55) * mm, "end": v(59.23, 24.96) * mm});
            skLineSegment(sketch, "E15.9.25.0", {"start": v(59.23, 24.96) * mm, "end": v(59.94, 23) * mm});
            skLineSegment(sketch, "E15.1.26.0", {"start": v(55.26, 21.92) * mm, "end": v(56.14, 22.71) * mm});
            skLineSegment(sketch, "E15.3.26.0", {"start": v(56.14, 22.71) * mm, "end": v(57.77, 21.43) * mm});
            skLineSegment(sketch, "E15.6.26.0", {"start": v(55.26, 21.92) * mm, "end": v(54.39, 21.13) * mm});
            skLineSegment(sketch, "E15.9.26.0", {"start": v(54.39, 21.13) * mm, "end": v(55.48, 19.38) * mm});
            skLineSegment(sketch, "E15.1.27.0", {"start": v(51.13, 17.34) * mm, "end": v(51.83, 18.3) * mm});
            skLineSegment(sketch, "E15.3.27.0", {"start": v(51.83, 18.3) * mm, "end": v(53.7, 17.38) * mm});
            skLineSegment(sketch, "E15.6.27.0", {"start": v(51.13, 17.34) * mm, "end": v(50.44, 16.39) * mm});
            skLineSegment(sketch, "E15.9.27.0", {"start": v(50.44, 16.39) * mm, "end": v(51.88, 14.9) * mm});
            skLineSegment(sketch, "E15.1.28.0", {"start": v(48.05, 12) * mm, "end": v(48.53, 13.07) * mm});
            skLineSegment(sketch, "E15.3.28.0", {"start": v(48.53, 13.07) * mm, "end": v(50.54, 12.57) * mm});
            skLineSegment(sketch, "E15.6.28.0", {"start": v(48.05, 12) * mm, "end": v(47.57, 10.92) * mm});
            skLineSegment(sketch, "E15.9.28.0", {"start": v(47.57, 10.92) * mm, "end": v(49.3, 9.76) * mm});
            skLineSegment(sketch, "E15.1.29.0", {"start": v(46.14, 6.13) * mm, "end": v(46.39, 7.29) * mm});
            skLineSegment(sketch, "E15.3.29.0", {"start": v(46.39, 7.29) * mm, "end": v(48.46, 7.21) * mm});
            skLineSegment(sketch, "E15.6.29.0", {"start": v(46.14, 6.13) * mm, "end": v(45.9, 4.98) * mm});
            skLineSegment(sketch, "E15.9.29.0", {"start": v(45.9, 4.98) * mm, "end": v(47.82, 4.2) * mm});
            skSolve(sketch);
        }
        {
            var Q0;
            Q0 = qSketchRegion(id + "F2", true);
            extrude(context, id + "F3", {"entities" : qUnion([Q0]), "depth" : 5 * mm, "offsetDistance" : 25 * mm});
        }
        {
            var Q0;
            Q0=makeQuery(id+"F3.opExtrude","CAP_FACE",FACE,{"disambiguationData":[OSD([sQuery(id+"F2.wireOp",EDGE,"E8"),sQuery(id+"F2.wireOp",EDGE,"E9"),sQuery(id+"F2.wireOp",EDGE,"E10"),sQuery(id+"F2.wireOp",EDGE,"E11.MirrorCS"),sQuery(id+"F2.wireOp",EDGE,"E12.MirrorCS"),sQuery(id+"F2.wireOp",EDGE,"E13.1.0"),sQuery(id+"F2.wireOp",EDGE,"E13.1.1"),sQuery(id+"F2.wireOp",EDGE,"E13.1.2"),sQuery(id+"F2.wireOp",EDGE,"E13.1.3"),sQuery(id+"F2.wireOp",EDGE,"E14.1.2.0"),sQuery(id+"F2.wireOp",EDGE,"E14.3.2.0"),sQuery(id+"F2.wireOp",EDGE,"E14.6.2.0"),sQuery(id+"F2.wireOp",EDGE,"E14.9.2.0"),sQuery(id+"F2.wireOp",EDGE,"E14.1.3.0"),sQuery(id+"F2.wireOp",EDGE,"E14.3.3.0"),sQuery(id+"F2.wireOp",EDGE,"E14.6.3.0"),sQuery(id+"F2.wireOp",EDGE,"E14.9.3.0"),sQuery(id+"F2.wireOp",EDGE,"E14.1.4.0"),sQuery(id+"F2.wireOp",EDGE,"E14.3.4.0"),sQuery(id+"F2.wireOp",EDGE,"E14.6.4.0"),sQuery(id+"F2.wireOp",EDGE,"E14.9.4.0"),sQuery(id+"F2.wireOp",EDGE,"E14.1.5.0"),sQuery(id+"F2.wireOp",EDGE,"E14.3.5.0"),sQuery(id+"F2.wireOp",EDGE,"E14.6.5.0"),sQuery(id+"F2.wireOp",EDGE,"E14.9.5.0"),sQuery(id+"F2.wireOp",EDGE,"E14.1.6.0"),sQuery(id+"F2.wireOp",EDGE,"E14.3.6.0"),sQuery(id+"F2.wireOp",EDGE,"E14.6.6.0"),sQuery(id+"F2.wireOp",EDGE,"E14.9.6.0"),sQuery(id+"F2.wireOp",EDGE,"E14.1.7.0"),sQuery(id+"F2.wireOp",EDGE,"E14.3.7.0"),sQuery(id+"F2.wireOp",EDGE,"E14.6.7.0"),sQuery(id+"F2.wireOp",EDGE,"E14.9.7.0"),sQuery(id+"F2.wireOp",EDGE,"E14.1.8.0"),sQuery(id+"F2.wireOp",EDGE,"E14.3.8.0"),sQuery(id+"F2.wireOp",EDGE,"E14.6.8.0"),sQuery(id+"F2.wireOp",EDGE,"E14.9.8.0"),sQuery(id+"F2.wireOp",EDGE,"E14.1.9.0"),sQuery(id+"F2.wireOp",EDGE,"E14.3.9.0"),sQuery(id+"F2.wireOp",EDGE,"E14.6.9.0"),sQuery(id+"F2.wireOp",EDGE,"E14.9.9.0"),sQuery(id+"F2.wireOp",EDGE,"E15.1.10.0"),sQuery(id+"F2.wireOp",EDGE,"E15.3.10.0"),sQuery(id+"F2.wireOp",EDGE,"E15.6.10.0"),sQuery(id+"F2.wireOp",EDGE,"E15.9.10.0"),sQuery(id+"F2.wireOp",EDGE,"E15.1.11.0"),sQuery(id+"F2.wireOp",EDGE,"E15.3.11.0"),sQuery(id+"F2.wireOp",EDGE,"E15.6.11.0"),sQuery(id+"F2.wireOp",EDGE,"E15.9.11.0"),sQuery(id+"F2.wireOp",EDGE,"E15.1.12.0"),sQuery(id+"F2.wireOp",EDGE,"E15.3.12.0"),sQuery(id+"F2.wireOp",EDGE,"E15.6.12.0"),sQuery(id+"F2.wireOp",EDGE,"E15.9.12.0"),sQuery(id+"F2.wireOp",EDGE,"E15.1.13.0"),sQuery(id+"F2.wireOp",EDGE,"E15.3.13.0"),sQuery(id+"F2.wireOp",EDGE,"E15.6.13.0"),sQuery(id+"F2.wireOp",EDGE,"E15.9.13.0"),sQuery(id+"F2.wireOp",EDGE,"E15.1.14.0"),sQuery(id+"F2.wireOp",EDGE,"E15.3.14.0"),sQuery(id+"F2.wireOp",EDGE,"E15.6.14.0"),sQuery(id+"F2.wireOp",EDGE,"E15.9.14.0"),sQuery(id+"F2.wireOp",EDGE,"E15.1.15.0"),sQuery(id+"F2.wireOp",EDGE,"E15.3.15.0"),sQuery(id+"F2.wireOp",EDGE,"E15.6.15.0"),sQuery(id+"F2.wireOp",EDGE,"E15.9.15.0"),sQuery(id+"F2.wireOp",EDGE,"E15.1.16.0"),sQuery(id+"F2.wireOp",EDGE,"E15.3.16.0"),sQuery(id+"F2.wireOp",EDGE,"E15.6.16.0"),sQuery(id+"F2.wireOp",EDGE,"E15.9.16.0"),sQuery(id+"F2.wireOp",EDGE,"E15.1.17.0"),sQuery(id+"F2.wireOp",EDGE,"E15.3.17.0"),sQuery(id+"F2.wireOp",EDGE,"E15.6.17.0"),sQuery(id+"F2.wireOp",EDGE,"E15.9.17.0"),sQuery(id+"F2.wireOp",EDGE,"E15.1.18.0"),sQuery(id+"F2.wireOp",EDGE,"E15.3.18.0"),sQuery(id+"F2.wireOp",EDGE,"E15.6.18.0"),sQuery(id+"F2.wireOp",EDGE,"E15.9.18.0"),sQuery(id+"F2.wireOp",EDGE,"E15.1.19.0"),sQuery(id+"F2.wireOp",EDGE,"E15.3.19.0"),sQuery(id+"F2.wireOp",EDGE,"E15.6.19.0"),sQuery(id+"F2.wireOp",EDGE,"E15.9.19.0"),sQuery(id+"F2.wireOp",EDGE,"E15.1.20.0"),sQuery(id+"F2.wireOp",EDGE,"E15.3.20.0"),sQuery(id+"F2.wireOp",EDGE,"E15.6.20.0"),sQuery(id+"F2.wireOp",EDGE,"E15.9.20.0"),sQuery(id+"F2.wireOp",EDGE,"E15.1.21.0"),sQuery(id+"F2.wireOp",EDGE,"E15.3.21.0"),sQuery(id+"F2.wireOp",EDGE,"E15.6.21.0"),sQuery(id+"F2.wireOp",EDGE,"E15.9.21.0"),sQuery(id+"F2.wireOp",EDGE,"E15.1.22.0"),sQuery(id+"F2.wireOp",EDGE,"E15.3.22.0"),sQuery(id+"F2.wireOp",EDGE,"E15.6.22.0"),sQuery(id+"F2.wireOp",EDGE,"E15.9.22.0"),sQuery(id+"F2.wireOp",EDGE,"E15.1.23.0"),sQuery(id+"F2.wireOp",EDGE,"E15.3.23.0"),sQuery(id+"F2.wireOp",EDGE,"E15.6.23.0"),sQuery(id+"F2.wireOp",EDGE,"E15.9.23.0"),sQuery(id+"F2.wireOp",EDGE,"E15.1.24.0"),sQuery(id+"F2.wireOp",EDGE,"E15.3.24.0"),sQuery(id+"F2.wireOp",EDGE,"E15.6.24.0"),sQuery(id+"F2.wireOp",EDGE,"E15.9.24.0"),sQuery(id+"F2.wireOp",EDGE,"E15.1.25.0"),sQuery(id+"F2.wireOp",EDGE,"E15.3.25.0"),sQuery(id+"F2.wireOp",EDGE,"E15.6.25.0"),sQuery(id+"F2.wireOp",EDGE,"E15.9.25.0"),sQuery(id+"F2.wireOp",EDGE,"E15.1.26.0"),sQuery(id+"F2.wireOp",EDGE,"E15.3.26.0"),sQuery(id+"F2.wireOp",EDGE,"E15.6.26.0"),sQuery(id+"F2.wireOp",EDGE,"E15.9.26.0"),sQuery(id+"F2.wireOp",EDGE,"E15.1.27.0"),sQuery(id+"F2.wireOp",EDGE,"E15.3.27.0"),sQuery(id+"F2.wireOp",EDGE,"E15.6.27.0"),sQuery(id+"F2.wireOp",EDGE,"E15.9.27.0"),sQuery(id+"F2.wireOp",EDGE,"E15.1.28.0"),sQuery(id+"F2.wireOp",EDGE,"E15.3.28.0"),sQuery(id+"F2.wireOp",EDGE,"E15.6.28.0"),sQuery(id+"F2.wireOp",EDGE,"E15.9.28.0"),sQuery(id+"F2.wireOp",EDGE,"E15.1.29.0"),sQuery(id+"F2.wireOp",EDGE,"E15.3.29.0"),sQuery(id+"F2.wireOp",EDGE,"E15.6.29.0"),sQuery(id+"F2.wireOp",EDGE,"E15.9.29.0")])],"isStart":true});
            var sketch = newSketch(context, id + "F4", { "sketchPlane" : qUnion([Q0])});
            skCircle(sketch, "E16", {"center": v(75, 0) * mm, "radius": 5 * mm});
            skSolve(sketch);
        }
        {
            var Q0;
            Q0 = qSketchRegion(id + "F4", true);
            extrude(context, id + "F5", {"entities" : qUnion([Q0]), "operationType" : NewBodyOperationType.ADD, "depth" : 15 * mm, "offsetDistance" : 25 * mm});
        }
        {
            var Q0;
            Q0=makeQuery(id+"F5.opExtrude","CAP_FACE",FACE,{"disambiguationData":[OSD([sQuery(id+"F4.wireOp",EDGE,"E16")])],"isStart":false});
            var sketch = newSketch(context, id + "F6", { "sketchPlane" : qUnion([Q0])});
            skLineSegment(sketch, "E17", {"start": v(-55, 22) * mm, "end": v(-55, -23) * mm});
            skLineSegment(sketch, "E18", {"start": v(-55, -23) * mm, "end": v(95, -23) * mm});
            skLineSegment(sketch, "E19", {"start": v(95, -23) * mm, "end": v(95, 22) * mm});
            skLineSegment(sketch, "E20", {"start": v(95, 22) * mm, "end": v(-55, 22) * mm});
            skSolve(sketch);
        }
        {
            var Q0;
            Q0 = qSketchRegion(id + "F6", true);
            extrude(context, id + "F7", {"entities" : qUnion([Q0]), "depth" : 10 * mm, "offsetDistance" : 25 * mm});
        }
        {
            var Q0;
            Q0=makeQuery(id+"F7.opExtrude","CAP_FACE",FACE,{"disambiguationData":[OSD([sQuery(id+"F6.wireOp",EDGE,"E17"),sQuery(id+"F6.wireOp",EDGE,"E18"),sQuery(id+"F6.wireOp",EDGE,"E19"),sQuery(id+"F6.wireOp",EDGE,"E20")])],"isStart":true});
            var sketch = newSketch(context, id + "F8", { "sketchPlane" : qUnion([Q0])});
            skCircle(sketch, "E21.0", {"center": v(75, 0) * mm, "radius": 5 * mm});
            skSolve(sketch);
        }
        {
            var Q0;
            Q0 = qSketchRegion(id + "F8", true);
            extrude(context, id + "F9", {"entities" : qUnion([Q0]), "operationType" : NewBodyOperationType.REMOVE, "oppositeDirection" : true, "depth" : 5 * mm, "offsetDistance" : 25 * mm});
        }
        {
            var Q0;
            Q0=makeQuery(id+"F7.opExtrude","CAP_FACE",FACE,{"disambiguationData":[OSD([sQuery(id+"F6.wireOp",EDGE,"E17"),sQuery(id+"F6.wireOp",EDGE,"E18"),sQuery(id+"F6.wireOp",EDGE,"E19"),sQuery(id+"F6.wireOp",EDGE,"E20")])],"isStart":true});
            var sketch = newSketch(context, id + "F10", { "sketchPlane" : qUnion([Q0])});
            skCircle(sketch, "E22", {"center": v(0, 0) * mm, "radius": 5 * mm});
            skSolve(sketch);
        }
        {
            var Q0;
            Q0 = qSketchRegion(id + "F10", true);
            extrude(context, id + "F11", {"entities" : qUnion([Q0]), "operationType" : NewBodyOperationType.REMOVE, "oppositeDirection" : true, "depth" : 5 * mm, "offsetDistance" : 25 * mm});
        }
        {
            var Q0;
            Q0=makeQuery(id+"F1.opExtrude","CAP_FACE",FACE,{"disambiguationData":[OSD([sQuery(id+"F0.wireOp",EDGE,"E0"),sQuery(id+"F0.wireOp",EDGE,"E1"),sQuery(id+"F0.wireOp",EDGE,"E2"),sQuery(id+"F0.wireOp",EDGE,"E3.MirrorCS"),sQuery(id+"F0.wireOp",EDGE,"E4.MirrorCS"),sQuery(id+"F0.wireOp",EDGE,"E5.1.0"),sQuery(id+"F0.wireOp",EDGE,"E5.1.1"),sQuery(id+"F0.wireOp",EDGE,"E5.1.2"),sQuery(id+"F0.wireOp",EDGE,"E5.1.3"),sQuery(id+"F0.wireOp",EDGE,"E5.2.0"),sQuery(id+"F0.wireOp",EDGE,"E5.2.1"),sQuery(id+"F0.wireOp",EDGE,"E5.2.2"),sQuery(id+"F0.wireOp",EDGE,"E5.2.3"),sQuery(id+"F0.wireOp",EDGE,"E6.2.3.0"),sQuery(id+"F0.wireOp",EDGE,"E6.3.3.0"),sQuery(id+"F0.wireOp",EDGE,"E6.6.3.0"),sQuery(id+"F0.wireOp",EDGE,"E6.9.3.0"),sQuery(id+"F0.wireOp",EDGE,"E6.2.4.0"),sQuery(id+"F0.wireOp",EDGE,"E6.3.4.0"),sQuery(id+"F0.wireOp",EDGE,"E6.6.4.0"),sQuery(id+"F0.wireOp",EDGE,"E6.9.4.0"),sQuery(id+"F0.wireOp",EDGE,"E6.2.5.0"),sQuery(id+"F0.wireOp",EDGE,"E6.3.5.0"),sQuery(id+"F0.wireOp",EDGE,"E6.6.5.0"),sQuery(id+"F0.wireOp",EDGE,"E6.9.5.0"),sQuery(id+"F0.wireOp",EDGE,"E6.2.6.0"),sQuery(id+"F0.wireOp",EDGE,"E6.3.6.0"),sQuery(id+"F0.wireOp",EDGE,"E6.6.6.0"),sQuery(id+"F0.wireOp",EDGE,"E6.9.6.0"),sQuery(id+"F0.wireOp",EDGE,"E6.2.7.0"),sQuery(id+"F0.wireOp",EDGE,"E6.3.7.0"),sQuery(id+"F0.wireOp",EDGE,"E6.6.7.0"),sQuery(id+"F0.wireOp",EDGE,"E6.9.7.0"),sQuery(id+"F0.wireOp",EDGE,"E6.2.8.0"),sQuery(id+"F0.wireOp",EDGE,"E6.3.8.0"),sQuery(id+"F0.wireOp",EDGE,"E6.6.8.0"),sQuery(id+"F0.wireOp",EDGE,"E6.9.8.0"),sQuery(id+"F0.wireOp",EDGE,"E6.2.9.0"),sQuery(id+"F0.wireOp",EDGE,"E6.3.9.0"),sQuery(id+"F0.wireOp",EDGE,"E6.6.9.0"),sQuery(id+"F0.wireOp",EDGE,"E6.9.9.0"),sQuery(id+"F0.wireOp",EDGE,"E6.2.10.0"),sQuery(id+"F0.wireOp",EDGE,"E6.3.10.0"),sQuery(id+"F0.wireOp",EDGE,"E6.6.10.0"),sQuery(id+"F0.wireOp",EDGE,"E6.9.10.0"),sQuery(id+"F0.wireOp",EDGE,"E6.2.11.0"),sQuery(id+"F0.wireOp",EDGE,"E6.3.11.0"),sQuery(id+"F0.wireOp",EDGE,"E6.6.11.0"),sQuery(id+"F0.wireOp",EDGE,"E6.9.11.0"),sQuery(id+"F0.wireOp",EDGE,"E6.2.12.0"),sQuery(id+"F0.wireOp",EDGE,"E6.3.12.0"),sQuery(id+"F0.wireOp",EDGE,"E6.6.12.0"),sQuery(id+"F0.wireOp",EDGE,"E6.9.12.0"),sQuery(id+"F0.wireOp",EDGE,"E6.2.13.0"),sQuery(id+"F0.wireOp",EDGE,"E6.3.13.0"),sQuery(id+"F0.wireOp",EDGE,"E6.6.13.0"),sQuery(id+"F0.wireOp",EDGE,"E6.9.13.0"),sQuery(id+"F0.wireOp",EDGE,"E6.2.14.0"),sQuery(id+"F0.wireOp",EDGE,"E6.3.14.0"),sQuery(id+"F0.wireOp",EDGE,"E6.6.14.0"),sQuery(id+"F0.wireOp",EDGE,"E6.9.14.0"),sQuery(id+"F0.wireOp",EDGE,"E6.2.15.0"),sQuery(id+"F0.wireOp",EDGE,"E6.3.15.0"),sQuery(id+"F0.wireOp",EDGE,"E6.6.15.0"),sQuery(id+"F0.wireOp",EDGE,"E6.9.15.0"),sQuery(id+"F0.wireOp",EDGE,"E6.2.16.0"),sQuery(id+"F0.wireOp",EDGE,"E6.3.16.0"),sQuery(id+"F0.wireOp",EDGE,"E6.6.16.0"),sQuery(id+"F0.wireOp",EDGE,"E6.9.16.0"),sQuery(id+"F0.wireOp",EDGE,"E6.2.17.0"),sQuery(id+"F0.wireOp",EDGE,"E6.3.17.0"),sQuery(id+"F0.wireOp",EDGE,"E6.6.17.0"),sQuery(id+"F0.wireOp",EDGE,"E6.9.17.0"),sQuery(id+"F0.wireOp",EDGE,"E6.2.18.0"),sQuery(id+"F0.wireOp",EDGE,"E6.3.18.0"),sQuery(id+"F0.wireOp",EDGE,"E6.6.18.0"),sQuery(id+"F0.wireOp",EDGE,"E6.9.18.0"),sQuery(id+"F0.wireOp",EDGE,"E6.2.19.0"),sQuery(id+"F0.wireOp",EDGE,"E6.3.19.0"),sQuery(id+"F0.wireOp",EDGE,"E6.6.19.0"),sQuery(id+"F0.wireOp",EDGE,"E6.9.19.0"),sQuery(id+"F0.wireOp",EDGE,"E6.2.20.0"),sQuery(id+"F0.wireOp",EDGE,"E6.3.20.0"),sQuery(id+"F0.wireOp",EDGE,"E6.6.20.0"),sQuery(id+"F0.wireOp",EDGE,"E6.9.20.0"),sQuery(id+"F0.wireOp",EDGE,"E6.2.21.0"),sQuery(id+"F0.wireOp",EDGE,"E6.3.21.0"),sQuery(id+"F0.wireOp",EDGE,"E6.6.21.0"),sQuery(id+"F0.wireOp",EDGE,"E6.9.21.0"),sQuery(id+"F0.wireOp",EDGE,"E6.2.22.0"),sQuery(id+"F0.wireOp",EDGE,"E6.3.22.0"),sQuery(id+"F0.wireOp",EDGE,"E6.6.22.0"),sQuery(id+"F0.wireOp",EDGE,"E6.9.22.0"),sQuery(id+"F0.wireOp",EDGE,"E6.2.23.0"),sQuery(id+"F0.wireOp",EDGE,"E6.3.23.0"),sQuery(id+"F0.wireOp",EDGE,"E6.6.23.0"),sQuery(id+"F0.wireOp",EDGE,"E6.9.23.0"),sQuery(id+"F0.wireOp",EDGE,"E6.2.24.0"),sQuery(id+"F0.wireOp",EDGE,"E6.3.24.0"),sQuery(id+"F0.wireOp",EDGE,"E6.6.24.0"),sQuery(id+"F0.wireOp",EDGE,"E6.9.24.0"),sQuery(id+"F0.wireOp",EDGE,"E6.2.25.0"),sQuery(id+"F0.wireOp",EDGE,"E6.3.25.0"),sQuery(id+"F0.wireOp",EDGE,"E6.6.25.0"),sQuery(id+"F0.wireOp",EDGE,"E6.9.25.0"),sQuery(id+"F0.wireOp",EDGE,"E6.2.26.0"),sQuery(id+"F0.wireOp",EDGE,"E6.3.26.0"),sQuery(id+"F0.wireOp",EDGE,"E6.6.26.0"),sQuery(id+"F0.wireOp",EDGE,"E6.9.26.0"),sQuery(id+"F0.wireOp",EDGE,"E6.2.27.0"),sQuery(id+"F0.wireOp",EDGE,"E6.3.27.0"),sQuery(id+"F0.wireOp",EDGE,"E6.6.27.0"),sQuery(id+"F0.wireOp",EDGE,"E6.9.27.0"),sQuery(id+"F0.wireOp",EDGE,"E6.2.28.0"),sQuery(id+"F0.wireOp",EDGE,"E6.3.28.0"),sQuery(id+"F0.wireOp",EDGE,"E6.6.28.0"),sQuery(id+"F0.wireOp",EDGE,"E6.9.28.0"),sQuery(id+"F0.wireOp",EDGE,"E6.2.29.0"),sQuery(id+"F0.wireOp",EDGE,"E6.3.29.0"),sQuery(id+"F0.wireOp",EDGE,"E6.6.29.0"),sQuery(id+"F0.wireOp",EDGE,"E6.9.29.0"),sQuery(id+"F0.wireOp",EDGE,"E7.2.30.0"),sQuery(id+"F0.wireOp",EDGE,"E7.3.30.0"),sQuery(id+"F0.wireOp",EDGE,"E7.6.30.0"),sQuery(id+"F0.wireOp",EDGE,"E7.9.30.0"),sQuery(id+"F0.wireOp",EDGE,"E7.2.31.0"),sQuery(id+"F0.wireOp",EDGE,"E7.3.31.0"),sQuery(id+"F0.wireOp",EDGE,"E7.6.31.0"),sQuery(id+"F0.wireOp",EDGE,"E7.9.31.0"),sQuery(id+"F0.wireOp",EDGE,"E7.2.32.0"),sQuery(id+"F0.wireOp",EDGE,"E7.3.32.0"),sQuery(id+"F0.wireOp",EDGE,"E7.6.32.0"),sQuery(id+"F0.wireOp",EDGE,"E7.9.32.0"),sQuery(id+"F0.wireOp",EDGE,"E7.2.33.0"),sQuery(id+"F0.wireOp",EDGE,"E7.3.33.0"),sQuery(id+"F0.wireOp",EDGE,"E7.6.33.0"),sQuery(id+"F0.wireOp",EDGE,"E7.9.33.0"),sQuery(id+"F0.wireOp",EDGE,"E7.2.34.0"),sQuery(id+"F0.wireOp",EDGE,"E7.3.34.0"),sQuery(id+"F0.wireOp",EDGE,"E7.6.34.0"),sQuery(id+"F0.wireOp",EDGE,"E7.9.34.0"),sQuery(id+"F0.wireOp",EDGE,"E7.2.35.0"),sQuery(id+"F0.wireOp",EDGE,"E7.3.35.0"),sQuery(id+"F0.wireOp",EDGE,"E7.6.35.0"),sQuery(id+"F0.wireOp",EDGE,"E7.9.35.0"),sQuery(id+"F0.wireOp",EDGE,"E7.2.36.0"),sQuery(id+"F0.wireOp",EDGE,"E7.3.36.0"),sQuery(id+"F0.wireOp",EDGE,"E7.6.36.0"),sQuery(id+"F0.wireOp",EDGE,"E7.9.36.0"),sQuery(id+"F0.wireOp",EDGE,"E7.2.37.0"),sQuery(id+"F0.wireOp",EDGE,"E7.3.37.0"),sQuery(id+"F0.wireOp",EDGE,"E7.6.37.0"),sQuery(id+"F0.wireOp",EDGE,"E7.9.37.0"),sQuery(id+"F0.wireOp",EDGE,"E7.2.38.0"),sQuery(id+"F0.wireOp",EDGE,"E7.3.38.0"),sQuery(id+"F0.wireOp",EDGE,"E7.6.38.0"),sQuery(id+"F0.wireOp",EDGE,"E7.9.38.0"),sQuery(id+"F0.wireOp",EDGE,"E7.2.39.0"),sQuery(id+"F0.wireOp",EDGE,"E7.3.39.0"),sQuery(id+"F0.wireOp",EDGE,"E7.6.39.0"),sQuery(id+"F0.wireOp",EDGE,"E7.9.39.0"),sQuery(id+"F0.wireOp",EDGE,"E7.2.40.0"),sQuery(id+"F0.wireOp",EDGE,"E7.3.40.0"),sQuery(id+"F0.wireOp",EDGE,"E7.6.40.0"),sQuery(id+"F0.wireOp",EDGE,"E7.9.40.0"),sQuery(id+"F0.wireOp",EDGE,"E7.2.41.0"),sQuery(id+"F0.wireOp",EDGE,"E7.3.41.0"),sQuery(id+"F0.wireOp",EDGE,"E7.6.41.0"),sQuery(id+"F0.wireOp",EDGE,"E7.9.41.0"),sQuery(id+"F0.wireOp",EDGE,"E7.2.42.0"),sQuery(id+"F0.wireOp",EDGE,"E7.3.42.0"),sQuery(id+"F0.wireOp",EDGE,"E7.6.42.0"),sQuery(id+"F0.wireOp",EDGE,"E7.9.42.0"),sQuery(id+"F0.wireOp",EDGE,"E7.2.43.0"),sQuery(id+"F0.wireOp",EDGE,"E7.3.43.0"),sQuery(id+"F0.wireOp",EDGE,"E7.6.43.0"),sQuery(id+"F0.wireOp",EDGE,"E7.9.43.0"),sQuery(id+"F0.wireOp",EDGE,"E7.2.44.0"),sQuery(id+"F0.wireOp",EDGE,"E7.3.44.0"),sQuery(id+"F0.wireOp",EDGE,"E7.6.44.0"),sQuery(id+"F0.wireOp",EDGE,"E7.9.44.0"),sQuery(id+"F0.wireOp",EDGE,"E7.2.45.0"),sQuery(id+"F0.wireOp",EDGE,"E7.3.45.0"),sQuery(id+"F0.wireOp",EDGE,"E7.6.45.0"),sQuery(id+"F0.wireOp",EDGE,"E7.9.45.0"),sQuery(id+"F0.wireOp",EDGE,"E7.2.46.0"),sQuery(id+"F0.wireOp",EDGE,"E7.3.46.0"),sQuery(id+"F0.wireOp",EDGE,"E7.6.46.0"),sQuery(id+"F0.wireOp",EDGE,"E7.9.46.0"),sQuery(id+"F0.wireOp",EDGE,"E7.2.47.0"),sQuery(id+"F0.wireOp",EDGE,"E7.3.47.0"),sQuery(id+"F0.wireOp",EDGE,"E7.6.47.0"),sQuery(id+"F0.wireOp",EDGE,"E7.9.47.0"),sQuery(id+"F0.wireOp",EDGE,"E7.2.48.0"),sQuery(id+"F0.wireOp",EDGE,"E7.3.48.0"),sQuery(id+"F0.wireOp",EDGE,"E7.6.48.0"),sQuery(id+"F0.wireOp",EDGE,"E7.9.48.0"),sQuery(id+"F0.wireOp",EDGE,"E7.2.49.0"),sQuery(id+"F0.wireOp",EDGE,"E7.3.49.0"),sQuery(id+"F0.wireOp",EDGE,"E7.6.49.0"),sQuery(id+"F0.wireOp",EDGE,"E7.9.49.0")])],"isStart":true});
            var sketch = newSketch(context, id + "F12", { "sketchPlane" : qUnion([Q0])});
            skCircle(sketch, "E23", {"center": v(0, 0) * mm, "radius": 5 * mm});
            skSolve(sketch);
        }
        {
            var Q0;
            Q0 = qSketchRegion(id + "F12", true);
            extrude(context, id + "F13", {"entities" : qUnion([Q0]), "operationType" : NewBodyOperationType.ADD, "depth" : 15 * mm, "offsetDistance" : 25 * mm});
        }
        {
            var Q0;
            Q0=makeQuery(id+"F1.opExtrude","CAP_FACE",FACE,{"disambiguationData":[OSD([sQuery(id+"F0.wireOp",EDGE,"E0"),sQuery(id+"F0.wireOp",EDGE,"E1"),sQuery(id+"F0.wireOp",EDGE,"E2"),sQuery(id+"F0.wireOp",EDGE,"E3.MirrorCS"),sQuery(id+"F0.wireOp",EDGE,"E4.MirrorCS"),sQuery(id+"F0.wireOp",EDGE,"E5.1.0"),sQuery(id+"F0.wireOp",EDGE,"E5.1.1"),sQuery(id+"F0.wireOp",EDGE,"E5.1.2"),sQuery(id+"F0.wireOp",EDGE,"E5.1.3"),sQuery(id+"F0.wireOp",EDGE,"E5.2.0"),sQuery(id+"F0.wireOp",EDGE,"E5.2.1"),sQuery(id+"F0.wireOp",EDGE,"E5.2.2"),sQuery(id+"F0.wireOp",EDGE,"E5.2.3"),sQuery(id+"F0.wireOp",EDGE,"E6.2.3.0"),sQuery(id+"F0.wireOp",EDGE,"E6.3.3.0"),sQuery(id+"F0.wireOp",EDGE,"E6.6.3.0"),sQuery(id+"F0.wireOp",EDGE,"E6.9.3.0"),sQuery(id+"F0.wireOp",EDGE,"E6.2.4.0"),sQuery(id+"F0.wireOp",EDGE,"E6.3.4.0"),sQuery(id+"F0.wireOp",EDGE,"E6.6.4.0"),sQuery(id+"F0.wireOp",EDGE,"E6.9.4.0"),sQuery(id+"F0.wireOp",EDGE,"E6.2.5.0"),sQuery(id+"F0.wireOp",EDGE,"E6.3.5.0"),sQuery(id+"F0.wireOp",EDGE,"E6.6.5.0"),sQuery(id+"F0.wireOp",EDGE,"E6.9.5.0"),sQuery(id+"F0.wireOp",EDGE,"E6.2.6.0"),sQuery(id+"F0.wireOp",EDGE,"E6.3.6.0"),sQuery(id+"F0.wireOp",EDGE,"E6.6.6.0"),sQuery(id+"F0.wireOp",EDGE,"E6.9.6.0"),sQuery(id+"F0.wireOp",EDGE,"E6.2.7.0"),sQuery(id+"F0.wireOp",EDGE,"E6.3.7.0"),sQuery(id+"F0.wireOp",EDGE,"E6.6.7.0"),sQuery(id+"F0.wireOp",EDGE,"E6.9.7.0"),sQuery(id+"F0.wireOp",EDGE,"E6.2.8.0"),sQuery(id+"F0.wireOp",EDGE,"E6.3.8.0"),sQuery(id+"F0.wireOp",EDGE,"E6.6.8.0"),sQuery(id+"F0.wireOp",EDGE,"E6.9.8.0"),sQuery(id+"F0.wireOp",EDGE,"E6.2.9.0"),sQuery(id+"F0.wireOp",EDGE,"E6.3.9.0"),sQuery(id+"F0.wireOp",EDGE,"E6.6.9.0"),sQuery(id+"F0.wireOp",EDGE,"E6.9.9.0"),sQuery(id+"F0.wireOp",EDGE,"E6.2.10.0"),sQuery(id+"F0.wireOp",EDGE,"E6.3.10.0"),sQuery(id+"F0.wireOp",EDGE,"E6.6.10.0"),sQuery(id+"F0.wireOp",EDGE,"E6.9.10.0"),sQuery(id+"F0.wireOp",EDGE,"E6.2.11.0"),sQuery(id+"F0.wireOp",EDGE,"E6.3.11.0"),sQuery(id+"F0.wireOp",EDGE,"E6.6.11.0"),sQuery(id+"F0.wireOp",EDGE,"E6.9.11.0"),sQuery(id+"F0.wireOp",EDGE,"E6.2.12.0"),sQuery(id+"F0.wireOp",EDGE,"E6.3.12.0"),sQuery(id+"F0.wireOp",EDGE,"E6.6.12.0"),sQuery(id+"F0.wireOp",EDGE,"E6.9.12.0"),sQuery(id+"F0.wireOp",EDGE,"E6.2.13.0"),sQuery(id+"F0.wireOp",EDGE,"E6.3.13.0"),sQuery(id+"F0.wireOp",EDGE,"E6.6.13.0"),sQuery(id+"F0.wireOp",EDGE,"E6.9.13.0"),sQuery(id+"F0.wireOp",EDGE,"E6.2.14.0"),sQuery(id+"F0.wireOp",EDGE,"E6.3.14.0"),sQuery(id+"F0.wireOp",EDGE,"E6.6.14.0"),sQuery(id+"F0.wireOp",EDGE,"E6.9.14.0"),sQuery(id+"F0.wireOp",EDGE,"E6.2.15.0"),sQuery(id+"F0.wireOp",EDGE,"E6.3.15.0"),sQuery(id+"F0.wireOp",EDGE,"E6.6.15.0"),sQuery(id+"F0.wireOp",EDGE,"E6.9.15.0"),sQuery(id+"F0.wireOp",EDGE,"E6.2.16.0"),sQuery(id+"F0.wireOp",EDGE,"E6.3.16.0"),sQuery(id+"F0.wireOp",EDGE,"E6.6.16.0"),sQuery(id+"F0.wireOp",EDGE,"E6.9.16.0"),sQuery(id+"F0.wireOp",EDGE,"E6.2.17.0"),sQuery(id+"F0.wireOp",EDGE,"E6.3.17.0"),sQuery(id+"F0.wireOp",EDGE,"E6.6.17.0"),sQuery(id+"F0.wireOp",EDGE,"E6.9.17.0"),sQuery(id+"F0.wireOp",EDGE,"E6.2.18.0"),sQuery(id+"F0.wireOp",EDGE,"E6.3.18.0"),sQuery(id+"F0.wireOp",EDGE,"E6.6.18.0"),sQuery(id+"F0.wireOp",EDGE,"E6.9.18.0"),sQuery(id+"F0.wireOp",EDGE,"E6.2.19.0"),sQuery(id+"F0.wireOp",EDGE,"E6.3.19.0"),sQuery(id+"F0.wireOp",EDGE,"E6.6.19.0"),sQuery(id+"F0.wireOp",EDGE,"E6.9.19.0"),sQuery(id+"F0.wireOp",EDGE,"E6.2.20.0"),sQuery(id+"F0.wireOp",EDGE,"E6.3.20.0"),sQuery(id+"F0.wireOp",EDGE,"E6.6.20.0"),sQuery(id+"F0.wireOp",EDGE,"E6.9.20.0"),sQuery(id+"F0.wireOp",EDGE,"E6.2.21.0"),sQuery(id+"F0.wireOp",EDGE,"E6.3.21.0"),sQuery(id+"F0.wireOp",EDGE,"E6.6.21.0"),sQuery(id+"F0.wireOp",EDGE,"E6.9.21.0"),sQuery(id+"F0.wireOp",EDGE,"E6.2.22.0"),sQuery(id+"F0.wireOp",EDGE,"E6.3.22.0"),sQuery(id+"F0.wireOp",EDGE,"E6.6.22.0"),sQuery(id+"F0.wireOp",EDGE,"E6.9.22.0"),sQuery(id+"F0.wireOp",EDGE,"E6.2.23.0"),sQuery(id+"F0.wireOp",EDGE,"E6.3.23.0"),sQuery(id+"F0.wireOp",EDGE,"E6.6.23.0"),sQuery(id+"F0.wireOp",EDGE,"E6.9.23.0"),sQuery(id+"F0.wireOp",EDGE,"E6.2.24.0"),sQuery(id+"F0.wireOp",EDGE,"E6.3.24.0"),sQuery(id+"F0.wireOp",EDGE,"E6.6.24.0"),sQuery(id+"F0.wireOp",EDGE,"E6.9.24.0"),sQuery(id+"F0.wireOp",EDGE,"E6.2.25.0"),sQuery(id+"F0.wireOp",EDGE,"E6.3.25.0"),sQuery(id+"F0.wireOp",EDGE,"E6.6.25.0"),sQuery(id+"F0.wireOp",EDGE,"E6.9.25.0"),sQuery(id+"F0.wireOp",EDGE,"E6.2.26.0"),sQuery(id+"F0.wireOp",EDGE,"E6.3.26.0"),sQuery(id+"F0.wireOp",EDGE,"E6.6.26.0"),sQuery(id+"F0.wireOp",EDGE,"E6.9.26.0"),sQuery(id+"F0.wireOp",EDGE,"E6.2.27.0"),sQuery(id+"F0.wireOp",EDGE,"E6.3.27.0"),sQuery(id+"F0.wireOp",EDGE,"E6.6.27.0"),sQuery(id+"F0.wireOp",EDGE,"E6.9.27.0"),sQuery(id+"F0.wireOp",EDGE,"E6.2.28.0"),sQuery(id+"F0.wireOp",EDGE,"E6.3.28.0"),sQuery(id+"F0.wireOp",EDGE,"E6.6.28.0"),sQuery(id+"F0.wireOp",EDGE,"E6.9.28.0"),sQuery(id+"F0.wireOp",EDGE,"E6.2.29.0"),sQuery(id+"F0.wireOp",EDGE,"E6.3.29.0"),sQuery(id+"F0.wireOp",EDGE,"E6.6.29.0"),sQuery(id+"F0.wireOp",EDGE,"E6.9.29.0"),sQuery(id+"F0.wireOp",EDGE,"E7.2.30.0"),sQuery(id+"F0.wireOp",EDGE,"E7.3.30.0"),sQuery(id+"F0.wireOp",EDGE,"E7.6.30.0"),sQuery(id+"F0.wireOp",EDGE,"E7.9.30.0"),sQuery(id+"F0.wireOp",EDGE,"E7.2.31.0"),sQuery(id+"F0.wireOp",EDGE,"E7.3.31.0"),sQuery(id+"F0.wireOp",EDGE,"E7.6.31.0"),sQuery(id+"F0.wireOp",EDGE,"E7.9.31.0"),sQuery(id+"F0.wireOp",EDGE,"E7.2.32.0"),sQuery(id+"F0.wireOp",EDGE,"E7.3.32.0"),sQuery(id+"F0.wireOp",EDGE,"E7.6.32.0"),sQuery(id+"F0.wireOp",EDGE,"E7.9.32.0"),sQuery(id+"F0.wireOp",EDGE,"E7.2.33.0"),sQuery(id+"F0.wireOp",EDGE,"E7.3.33.0"),sQuery(id+"F0.wireOp",EDGE,"E7.6.33.0"),sQuery(id+"F0.wireOp",EDGE,"E7.9.33.0"),sQuery(id+"F0.wireOp",EDGE,"E7.2.34.0"),sQuery(id+"F0.wireOp",EDGE,"E7.3.34.0"),sQuery(id+"F0.wireOp",EDGE,"E7.6.34.0"),sQuery(id+"F0.wireOp",EDGE,"E7.9.34.0"),sQuery(id+"F0.wireOp",EDGE,"E7.2.35.0"),sQuery(id+"F0.wireOp",EDGE,"E7.3.35.0"),sQuery(id+"F0.wireOp",EDGE,"E7.6.35.0"),sQuery(id+"F0.wireOp",EDGE,"E7.9.35.0"),sQuery(id+"F0.wireOp",EDGE,"E7.2.36.0"),sQuery(id+"F0.wireOp",EDGE,"E7.3.36.0"),sQuery(id+"F0.wireOp",EDGE,"E7.6.36.0"),sQuery(id+"F0.wireOp",EDGE,"E7.9.36.0"),sQuery(id+"F0.wireOp",EDGE,"E7.2.37.0"),sQuery(id+"F0.wireOp",EDGE,"E7.3.37.0"),sQuery(id+"F0.wireOp",EDGE,"E7.6.37.0"),sQuery(id+"F0.wireOp",EDGE,"E7.9.37.0"),sQuery(id+"F0.wireOp",EDGE,"E7.2.38.0"),sQuery(id+"F0.wireOp",EDGE,"E7.3.38.0"),sQuery(id+"F0.wireOp",EDGE,"E7.6.38.0"),sQuery(id+"F0.wireOp",EDGE,"E7.9.38.0"),sQuery(id+"F0.wireOp",EDGE,"E7.2.39.0"),sQuery(id+"F0.wireOp",EDGE,"E7.3.39.0"),sQuery(id+"F0.wireOp",EDGE,"E7.6.39.0"),sQuery(id+"F0.wireOp",EDGE,"E7.9.39.0"),sQuery(id+"F0.wireOp",EDGE,"E7.2.40.0"),sQuery(id+"F0.wireOp",EDGE,"E7.3.40.0"),sQuery(id+"F0.wireOp",EDGE,"E7.6.40.0"),sQuery(id+"F0.wireOp",EDGE,"E7.9.40.0"),sQuery(id+"F0.wireOp",EDGE,"E7.2.41.0"),sQuery(id+"F0.wireOp",EDGE,"E7.3.41.0"),sQuery(id+"F0.wireOp",EDGE,"E7.6.41.0"),sQuery(id+"F0.wireOp",EDGE,"E7.9.41.0"),sQuery(id+"F0.wireOp",EDGE,"E7.2.42.0"),sQuery(id+"F0.wireOp",EDGE,"E7.3.42.0"),sQuery(id+"F0.wireOp",EDGE,"E7.6.42.0"),sQuery(id+"F0.wireOp",EDGE,"E7.9.42.0"),sQuery(id+"F0.wireOp",EDGE,"E7.2.43.0"),sQuery(id+"F0.wireOp",EDGE,"E7.3.43.0"),sQuery(id+"F0.wireOp",EDGE,"E7.6.43.0"),sQuery(id+"F0.wireOp",EDGE,"E7.9.43.0"),sQuery(id+"F0.wireOp",EDGE,"E7.2.44.0"),sQuery(id+"F0.wireOp",EDGE,"E7.3.44.0"),sQuery(id+"F0.wireOp",EDGE,"E7.6.44.0"),sQuery(id+"F0.wireOp",EDGE,"E7.9.44.0"),sQuery(id+"F0.wireOp",EDGE,"E7.2.45.0"),sQuery(id+"F0.wireOp",EDGE,"E7.3.45.0"),sQuery(id+"F0.wireOp",EDGE,"E7.6.45.0"),sQuery(id+"F0.wireOp",EDGE,"E7.9.45.0"),sQuery(id+"F0.wireOp",EDGE,"E7.2.46.0"),sQuery(id+"F0.wireOp",EDGE,"E7.3.46.0"),sQuery(id+"F0.wireOp",EDGE,"E7.6.46.0"),sQuery(id+"F0.wireOp",EDGE,"E7.9.46.0"),sQuery(id+"F0.wireOp",EDGE,"E7.2.47.0"),sQuery(id+"F0.wireOp",EDGE,"E7.3.47.0"),sQuery(id+"F0.wireOp",EDGE,"E7.6.47.0"),sQuery(id+"F0.wireOp",EDGE,"E7.9.47.0"),sQuery(id+"F0.wireOp",EDGE,"E7.2.48.0"),sQuery(id+"F0.wireOp",EDGE,"E7.3.48.0"),sQuery(id+"F0.wireOp",EDGE,"E7.6.48.0"),sQuery(id+"F0.wireOp",EDGE,"E7.9.48.0"),sQuery(id+"F0.wireOp",EDGE,"E7.2.49.0"),sQuery(id+"F0.wireOp",EDGE,"E7.3.49.0"),sQuery(id+"F0.wireOp",EDGE,"E7.6.49.0"),sQuery(id+"F0.wireOp",EDGE,"E7.9.49.0")])],"isStart":false});
            var sketch = newSketch(context, id + "F14", { "sketchPlane" : qUnion([Q0])});
            skCircle(sketch, "E24", {"center": v(0, 0) * mm, "radius": 5 * mm});
            skSolve(sketch);
        }
        {
            var Q0;
            Q0 = qSketchRegion(id + "F14", true);
            extrude(context, id + "F15", {"entities" : qUnion([Q0]), "operationType" : NewBodyOperationType.ADD, "depth" : 50 * mm, "offsetDistance" : 25 * mm});
        }
        {
            var Q0;
            Q0=makeQuery(id+"F15.opExtrude","CAP_FACE",FACE,{"disambiguationData":[OSD([sQuery(id+"F14.wireOp",EDGE,"E24")])],"isStart":false});
            var sketch = newSketch(context, id + "F16", { "sketchPlane" : qUnion([Q0])});
            skCircle(sketch, "E25", {"center": v(0, 0) * mm, "radius": 15 * mm});
            skLineSegment(sketch, "E26", {"start": v(0, 45) * mm, "end": v(5, 45) * mm});
            skLineSegment(sketch, "E27", {"start": v(5, 45) * mm, "end": v(11.17, 10.01) * mm});
            skLineSegment(sketch, "E28.MirrorCS", {"start": v(0, 45) * mm, "end": v(-5, 45) * mm});
            skLineSegment(sketch, "E29.MirrorCS", {"start": v(-5, 45) * mm, "end": v(-11.17, 10.01) * mm});
            skLineSegment(sketch, "E30.1.0", {"start": v(-36.47, -26.83) * mm, "end": v(-3.09, -14.68) * mm});
            skLineSegment(sketch, "E30.1.1", {"start": v(-38.97, -22.5) * mm, "end": v(-36.47, -26.83) * mm});
            skLineSegment(sketch, "E30.1.2", {"start": v(-38.97, -22.5) * mm, "end": v(-41.47, -18.17) * mm});
            skLineSegment(sketch, "E30.1.3", {"start": v(-41.47, -18.17) * mm, "end": v(-14.26, 4.67) * mm});
            skLineSegment(sketch, "E30.2.0", {"start": v(41.47, -18.17) * mm, "end": v(14.26, 4.67) * mm});
            skLineSegment(sketch, "E30.2.1", {"start": v(38.97, -22.5) * mm, "end": v(41.47, -18.17) * mm});
            skLineSegment(sketch, "E30.2.2", {"start": v(38.97, -22.5) * mm, "end": v(36.47, -26.83) * mm});
            skLineSegment(sketch, "E30.2.3", {"start": v(36.47, -26.83) * mm, "end": v(3.09, -14.68) * mm});
            skSolve(sketch);
        }
        {
            var Q0;
            Q0 = qSketchRegion(id + "F16", true);
            extrude(context, id + "F17", {"entities" : qUnion([Q0]), "operationType" : NewBodyOperationType.ADD, "depth" : 5 * mm, "offsetDistance" : 25 * mm});
        }
        {
            var Q0;
            Q0=makeQuery(id+"F3.opExtrude","CAP_FACE",FACE,{"disambiguationData":[OSD([sQuery(id+"F2.wireOp",EDGE,"E8"),sQuery(id+"F2.wireOp",EDGE,"E9"),sQuery(id+"F2.wireOp",EDGE,"E10"),sQuery(id+"F2.wireOp",EDGE,"E11.MirrorCS"),sQuery(id+"F2.wireOp",EDGE,"E12.MirrorCS"),sQuery(id+"F2.wireOp",EDGE,"E13.1.0"),sQuery(id+"F2.wireOp",EDGE,"E13.1.1"),sQuery(id+"F2.wireOp",EDGE,"E13.1.2"),sQuery(id+"F2.wireOp",EDGE,"E13.1.3"),sQuery(id+"F2.wireOp",EDGE,"E14.1.2.0"),sQuery(id+"F2.wireOp",EDGE,"E14.3.2.0"),sQuery(id+"F2.wireOp",EDGE,"E14.6.2.0"),sQuery(id+"F2.wireOp",EDGE,"E14.9.2.0"),sQuery(id+"F2.wireOp",EDGE,"E14.1.3.0"),sQuery(id+"F2.wireOp",EDGE,"E14.3.3.0"),sQuery(id+"F2.wireOp",EDGE,"E14.6.3.0"),sQuery(id+"F2.wireOp",EDGE,"E14.9.3.0"),sQuery(id+"F2.wireOp",EDGE,"E14.1.4.0"),sQuery(id+"F2.wireOp",EDGE,"E14.3.4.0"),sQuery(id+"F2.wireOp",EDGE,"E14.6.4.0"),sQuery(id+"F2.wireOp",EDGE,"E14.9.4.0"),sQuery(id+"F2.wireOp",EDGE,"E14.1.5.0"),sQuery(id+"F2.wireOp",EDGE,"E14.3.5.0"),sQuery(id+"F2.wireOp",EDGE,"E14.6.5.0"),sQuery(id+"F2.wireOp",EDGE,"E14.9.5.0"),sQuery(id+"F2.wireOp",EDGE,"E14.1.6.0"),sQuery(id+"F2.wireOp",EDGE,"E14.3.6.0"),sQuery(id+"F2.wireOp",EDGE,"E14.6.6.0"),sQuery(id+"F2.wireOp",EDGE,"E14.9.6.0"),sQuery(id+"F2.wireOp",EDGE,"E14.1.7.0"),sQuery(id+"F2.wireOp",EDGE,"E14.3.7.0"),sQuery(id+"F2.wireOp",EDGE,"E14.6.7.0"),sQuery(id+"F2.wireOp",EDGE,"E14.9.7.0"),sQuery(id+"F2.wireOp",EDGE,"E14.1.8.0"),sQuery(id+"F2.wireOp",EDGE,"E14.3.8.0"),sQuery(id+"F2.wireOp",EDGE,"E14.6.8.0"),sQuery(id+"F2.wireOp",EDGE,"E14.9.8.0"),sQuery(id+"F2.wireOp",EDGE,"E14.1.9.0"),sQuery(id+"F2.wireOp",EDGE,"E14.3.9.0"),sQuery(id+"F2.wireOp",EDGE,"E14.6.9.0"),sQuery(id+"F2.wireOp",EDGE,"E14.9.9.0"),sQuery(id+"F2.wireOp",EDGE,"E15.1.10.0"),sQuery(id+"F2.wireOp",EDGE,"E15.3.10.0"),sQuery(id+"F2.wireOp",EDGE,"E15.6.10.0"),sQuery(id+"F2.wireOp",EDGE,"E15.9.10.0"),sQuery(id+"F2.wireOp",EDGE,"E15.1.11.0"),sQuery(id+"F2.wireOp",EDGE,"E15.3.11.0"),sQuery(id+"F2.wireOp",EDGE,"E15.6.11.0"),sQuery(id+"F2.wireOp",EDGE,"E15.9.11.0"),sQuery(id+"F2.wireOp",EDGE,"E15.1.12.0"),sQuery(id+"F2.wireOp",EDGE,"E15.3.12.0"),sQuery(id+"F2.wireOp",EDGE,"E15.6.12.0"),sQuery(id+"F2.wireOp",EDGE,"E15.9.12.0"),sQuery(id+"F2.wireOp",EDGE,"E15.1.13.0"),sQuery(id+"F2.wireOp",EDGE,"E15.3.13.0"),sQuery(id+"F2.wireOp",EDGE,"E15.6.13.0"),sQuery(id+"F2.wireOp",EDGE,"E15.9.13.0"),sQuery(id+"F2.wireOp",EDGE,"E15.1.14.0"),sQuery(id+"F2.wireOp",EDGE,"E15.3.14.0"),sQuery(id+"F2.wireOp",EDGE,"E15.6.14.0"),sQuery(id+"F2.wireOp",EDGE,"E15.9.14.0"),sQuery(id+"F2.wireOp",EDGE,"E15.1.15.0"),sQuery(id+"F2.wireOp",EDGE,"E15.3.15.0"),sQuery(id+"F2.wireOp",EDGE,"E15.6.15.0"),sQuery(id+"F2.wireOp",EDGE,"E15.9.15.0"),sQuery(id+"F2.wireOp",EDGE,"E15.1.16.0"),sQuery(id+"F2.wireOp",EDGE,"E15.3.16.0"),sQuery(id+"F2.wireOp",EDGE,"E15.6.16.0"),sQuery(id+"F2.wireOp",EDGE,"E15.9.16.0"),sQuery(id+"F2.wireOp",EDGE,"E15.1.17.0"),sQuery(id+"F2.wireOp",EDGE,"E15.3.17.0"),sQuery(id+"F2.wireOp",EDGE,"E15.6.17.0"),sQuery(id+"F2.wireOp",EDGE,"E15.9.17.0"),sQuery(id+"F2.wireOp",EDGE,"E15.1.18.0"),sQuery(id+"F2.wireOp",EDGE,"E15.3.18.0"),sQuery(id+"F2.wireOp",EDGE,"E15.6.18.0"),sQuery(id+"F2.wireOp",EDGE,"E15.9.18.0"),sQuery(id+"F2.wireOp",EDGE,"E15.1.19.0"),sQuery(id+"F2.wireOp",EDGE,"E15.3.19.0"),sQuery(id+"F2.wireOp",EDGE,"E15.6.19.0"),sQuery(id+"F2.wireOp",EDGE,"E15.9.19.0"),sQuery(id+"F2.wireOp",EDGE,"E15.1.20.0"),sQuery(id+"F2.wireOp",EDGE,"E15.3.20.0"),sQuery(id+"F2.wireOp",EDGE,"E15.6.20.0"),sQuery(id+"F2.wireOp",EDGE,"E15.9.20.0"),sQuery(id+"F2.wireOp",EDGE,"E15.1.21.0"),sQuery(id+"F2.wireOp",EDGE,"E15.3.21.0"),sQuery(id+"F2.wireOp",EDGE,"E15.6.21.0"),sQuery(id+"F2.wireOp",EDGE,"E15.9.21.0"),sQuery(id+"F2.wireOp",EDGE,"E15.1.22.0"),sQuery(id+"F2.wireOp",EDGE,"E15.3.22.0"),sQuery(id+"F2.wireOp",EDGE,"E15.6.22.0"),sQuery(id+"F2.wireOp",EDGE,"E15.9.22.0"),sQuery(id+"F2.wireOp",EDGE,"E15.1.23.0"),sQuery(id+"F2.wireOp",EDGE,"E15.3.23.0"),sQuery(id+"F2.wireOp",EDGE,"E15.6.23.0"),sQuery(id+"F2.wireOp",EDGE,"E15.9.23.0"),sQuery(id+"F2.wireOp",EDGE,"E15.1.24.0"),sQuery(id+"F2.wireOp",EDGE,"E15.3.24.0"),sQuery(id+"F2.wireOp",EDGE,"E15.6.24.0"),sQuery(id+"F2.wireOp",EDGE,"E15.9.24.0"),sQuery(id+"F2.wireOp",EDGE,"E15.1.25.0"),sQuery(id+"F2.wireOp",EDGE,"E15.3.25.0"),sQuery(id+"F2.wireOp",EDGE,"E15.6.25.0"),sQuery(id+"F2.wireOp",EDGE,"E15.9.25.0"),sQuery(id+"F2.wireOp",EDGE,"E15.1.26.0"),sQuery(id+"F2.wireOp",EDGE,"E15.3.26.0"),sQuery(id+"F2.wireOp",EDGE,"E15.6.26.0"),sQuery(id+"F2.wireOp",EDGE,"E15.9.26.0"),sQuery(id+"F2.wireOp",EDGE,"E15.1.27.0"),sQuery(id+"F2.wireOp",EDGE,"E15.3.27.0"),sQuery(id+"F2.wireOp",EDGE,"E15.6.27.0"),sQuery(id+"F2.wireOp",EDGE,"E15.9.27.0"),sQuery(id+"F2.wireOp",EDGE,"E15.1.28.0"),sQuery(id+"F2.wireOp",EDGE,"E15.3.28.0"),sQuery(id+"F2.wireOp",EDGE,"E15.6.28.0"),sQuery(id+"F2.wireOp",EDGE,"E15.9.28.0"),sQuery(id+"F2.wireOp",EDGE,"E15.1.29.0"),sQuery(id+"F2.wireOp",EDGE,"E15.3.29.0"),sQuery(id+"F2.wireOp",EDGE,"E15.6.29.0"),sQuery(id+"F2.wireOp",EDGE,"E15.9.29.0")])],"isStart":false});
            var sketch = newSketch(context, id + "F18", { "sketchPlane" : qUnion([Q0])});
            skCircle(sketch, "E31", {"center": v(75, 0) * mm, "radius": 5 * mm});
            skSolve(sketch);
        }
        {
            var Q0;
            Q0 = qSketchRegion(id + "F18", true);
            extrude(context, id + "F19", {"entities" : qUnion([Q0]), "operationType" : NewBodyOperationType.ADD, "depth" : 3 * mm, "offsetDistance" : 25 * mm});
        }
        {
            var Q0;
            Q0=makeQuery(id+"F19.opExtrude","CAP_FACE",FACE,{"disambiguationData":[OSD([sQuery(id+"F18.wireOp",EDGE,"E31")])],"isStart":false});
            var sketch = newSketch(context, id + "F20", { "sketchPlane" : qUnion([Q0])});
            skCircle(sketch, "E32", {"center": v(75, 0) * mm, "radius": 7.5 * mm});
            skLineSegment(sketch, "E33", {"start": v(80.6, 5) * mm, "end": v(95.6, 5) * mm});
            skLineSegment(sketch, "E34", {"start": v(95.6, 5) * mm, "end": v(95.6, 0) * mm});
            skLineSegment(sketch, "E35.MirrorCS", {"start": v(80.6, -5) * mm, "end": v(95.6, -5) * mm});
            skLineSegment(sketch, "E36.MirrorCS", {"start": v(95.6, -5) * mm, "end": v(95.6, 0) * mm});
            skSolve(sketch);
        }
        {
            var Q0;
            Q0 = qSketchRegion(id + "F20", true);
            extrude(context, id + "F21", {"entities" : qUnion([Q0]), "operationType" : NewBodyOperationType.ADD, "depth" : 5 * mm, "offsetDistance" : 25 * mm});
        }
        {
            var Q0;
            Q0=makeQuery(id+"F17.opExtrude","CAP_EDGE",EDGE,{"disambiguationData":[OSD([sQuery(id+"F16.wireOp",EDGE,"E27")])],"isStart":false});
            var Q1;
            Q1=makeQuery(id+"F17.opExtrude","CAP_EDGE",EDGE,{"disambiguationData":[OSD([sQuery(id+"F16.wireOp",EDGE,"E30.2.3")])],"isStart":false});
            var Q2;
            Q2=makeQuery(id+"F17.opExtrude","CAP_EDGE",EDGE,{"disambiguationData":[OSD([sQuery(id+"F16.wireOp",EDGE,"E30.1.3")])],"isStart":false});
            chamfer(context, id + "F22", {"entities" : qUnion([Q0, Q1, Q2]), "width" : 5 * mm, "tangentPropagation" : true});
        }
        {
            var Q0;
            Q0=makeQuery(id+"F17.opExtrude","CAP_FACE",FACE,{"disambiguationData":[OSD([sQuery(id+"F16.wireOp",EDGE,"E25"),sQuery(id+"F16.wireOp",EDGE,"E26"),sQuery(id+"F16.wireOp",EDGE,"E27"),sQuery(id+"F16.wireOp",EDGE,"E28.MirrorCS"),sQuery(id+"F16.wireOp",EDGE,"E29.MirrorCS"),sQuery(id+"F16.wireOp",EDGE,"E30.1.0"),sQuery(id+"F16.wireOp",EDGE,"E30.1.1"),sQuery(id+"F16.wireOp",EDGE,"E30.1.2"),sQuery(id+"F16.wireOp",EDGE,"E30.1.3"),sQuery(id+"F16.wireOp",EDGE,"E30.2.0"),sQuery(id+"F16.wireOp",EDGE,"E30.2.1"),sQuery(id+"F16.wireOp",EDGE,"E30.2.2"),sQuery(id+"F16.wireOp",EDGE,"E30.2.3")])],"isStart":false});
            var sketch = newSketch(context, id + "F23", { "sketchPlane" : qUnion([Q0])});
            skLineSegment(sketch, "E37.bottom", {"start": v(-3, 37) * mm, "end": v(0, 37) * mm});
            skLineSegment(sketch, "E37.top", {"start": v(-3, 22) * mm, "end": v(0, 22) * mm});
            skLineSegment(sketch, "E37.left", {"start": v(-3, 37) * mm, "end": v(-3, 22) * mm});
            skLineSegment(sketch, "E37.right", {"start": v(0, 37) * mm, "end": v(0, 22) * mm});
            skLineSegment(sketch, "E38.1.0", {"start": v(-30.54, -21.1) * mm, "end": v(-17.55, -13.6) * mm});
            skLineSegment(sketch, "E38.1.1", {"start": v(-30.54, -21.1) * mm, "end": v(-32.04, -18.5) * mm});
            skLineSegment(sketch, "E38.1.2", {"start": v(-32.04, -18.5) * mm, "end": v(-19.05, -11) * mm});
            skLineSegment(sketch, "E38.1.3", {"start": v(-17.55, -13.6) * mm, "end": v(-19.05, -11) * mm});
            skLineSegment(sketch, "E38.2.0", {"start": v(33.54, -15.9) * mm, "end": v(20.55, -8.4) * mm});
            skLineSegment(sketch, "E38.2.1", {"start": v(33.54, -15.9) * mm, "end": v(32.04, -18.5) * mm});
            skLineSegment(sketch, "E38.2.2", {"start": v(32.04, -18.5) * mm, "end": v(19.05, -11) * mm});
            skLineSegment(sketch, "E38.2.3", {"start": v(20.55, -8.4) * mm, "end": v(19.05, -11) * mm});
            skPoint(sketch, "E38.center", {"position": v(0, 0) * mm});
            skSolve(sketch);
        }
        {
            var Q0;
            Q0 = qSketchRegion(id + "F23", true);
            extrude(context, id + "F24", {"entities" : qUnion([Q0]), "operationType" : NewBodyOperationType.REMOVE, "oppositeDirection" : true, "depth" : 3 * mm, "offsetDistance" : 25 * mm});
        }
        {
            var Q0;
            Q0=qCreatedBy(makeId("Top.planeOp"),FACE);
            var sketch = newSketch(context, id + "F25", { "sketchPlane" : qUnion([Q0])});
            skLineSegment(sketch, "E39.bottom", {"start": v(-43, 70) * mm, "end": v(-40, 70) * mm});
            skLineSegment(sketch, "E39.top", {"start": v(-43, 55) * mm, "end": v(-40, 55) * mm});
            skLineSegment(sketch, "E39.left", {"start": v(-43, 70) * mm, "end": v(-43, 55) * mm});
            skLineSegment(sketch, "E39.right", {"start": v(-40, 70) * mm, "end": v(-40, 55) * mm});
            skSolve(sketch);
        }
        {
            var Q0;
            Q0 = qSketchRegion(id + "F25", true);
            extrude(context, id + "F26", {"entities" : qUnion([Q0]), "depth" : 5 * mm, "offsetDistance" : 25 * mm});
        }
    });
